FCSTD DOCUMENT  (FreeCAD 0.21R33694 (Git))
Label: merged-carcasa-final
License: Creative Commons Attribution-NonCommercial-ShareAlike 4.0
LicenseURL: https://creativecommons.org/licenses/by-nc-sa/4.0/
objects: TechDraw::DrawViewDimension×81, Part::Box×29, Part::Fuse×24, Part::Cut×21, TechDraw::DrawViewPart×20, Part::Feature×15, TechDraw::DrawViewBalloon×12, Part::Mirroring×11, Part::Chamfer×9, Part::Cylinder×6, Part::Fillet×5, TechDraw::DrawSVGTemplate×5, TechDraw::DrawPage×5, App::DocumentObjectGroup×5, Sketcher::SketchObject×4, Part::Extrusion×4, Part::Compound×3, TechDraw::DrawViewAnnotation×3, Part::MultiFuse×2, Part::FeaturePython×2, +5 more types
note: 228 computed .brp shape members not serialized (recipe doc carries the construction recipe); baked Part::Feature solids carry a one-line shape summary decoded from their .brp

FEATURE [Sketcher::SketchObject] Sketch  label="case-taladros"
  FullyConstrained = true
  MapMode = 5
  Support = -> [XY_Plane]
  sketch-geometry (4):
    g0: LineSegment StartX=-50 StartY=85 StartZ=0 EndX=50 EndY=85 EndZ=0
    g1: LineSegment StartX=50 StartY=85 StartZ=0 EndX=50 EndY=-85 EndZ=0
    g2: LineSegment StartX=50 StartY=-85 StartZ=0 EndX=-50 EndY=-85 EndZ=0
    g3: LineSegment StartX=-50 StartY=-85 StartZ=0 EndX=-50 EndY=85 EndZ=0
  constraints (10):
    c: Coincident(g0,g1)
    c: Coincident(g1,g2)
    c: Coincident(g2,g3)
    c: Coincident(g3,g0)
    c: Horizontal(g2)
    c: Vertical(g1)
    c: Symmetric(g0,g0,g-2)
    c: Symmetric(g2,g0,g-1)
    c: DistanceY(g3,g3) = 170
    c: DistanceX(g0,g0) = 100
FEATURE [Part::Box] Box001  label="vaciado"
  AttacherType = Attacher::AttachEngine3D
  Height = 42
  Length = 94
  Placement = pos=(-47,-76,3) rot=(0,0,1;0rad)
  Width = 152
FEATURE [Sketcher::SketchObject] Sketch008  label="tapa-taladros"
  FullyConstrained = true
  MapMode = 5
  sketch-geometry (4):
    g0: LineSegment StartX=-49 StartY=84 StartZ=0 EndX=49 EndY=84 EndZ=0
    g1: LineSegment StartX=49 StartY=84 StartZ=0 EndX=49 EndY=-84 EndZ=0
    g2: LineSegment StartX=49 StartY=-84 StartZ=0 EndX=-49 EndY=-84 EndZ=0
    g3: LineSegment StartX=-49 StartY=-84 StartZ=0 EndX=-49 EndY=84 EndZ=0
  constraints (10):
    c: Coincident(g0,g1)
    c: Coincident(g1,g2)
    c: Coincident(g2,g3)
    c: Coincident(g3,g0)
    c: Horizontal(g2)
    c: Vertical(g1)
    c: Symmetric(g0,g0,g-2)
    c: Symmetric(g2,g0,g-1)
    c: DistanceY(g3,g3) = 168
    c: DistanceX(g0,g0) = 98
FEATURE [Part::Box] Box010  label="restriccion-lipo"
  AttacherType = Attacher::AttachEngine3D
  Height = 38
  Length = 5
  Placement = pos=(17,-75,5) rot=(0,0,1;0rad)
  Width = 73
FEATURE [Part::Box] Box011  label="restriccion-lipo001"
  AttacherType = Attacher::AttachEngine3D
  Height = 18
  Length = 7
  Placement = pos=(16,-60,14) rot=(0,0,1;0rad)
  Width = 43
FEATURE [Part::Cut] Cut028
  Base = -> Box010
  Refine = true
  Tool = -> Box011
FEATURE [Part::Chamfer] Chamfer002
  Base = -> Cut028
  Edges = 2 edges r=3: [Edge2,Edge4]
FEATURE [Part::Chamfer] Chamfer003
  Base = -> Chamfer002
  Edges = 4 edges r=2: [Edge5,Edge6,Edge7,Edge8]
FEATURE [Part::Box] Box012  label="Cube004"
  AttacherType = Attacher::AttachEngine3D
  Height = 5
  Length = 20
  Placement = pos=(20,-4,16) rot=(0,0,1;0rad)
  Width = 2
FEATURE [Part::Fuse] Fusion001032  label="rejillas-lipo"
  Base = -> Chamfer003
  Placement = pos=(7,2,-2) rot=(0,0,1;0rad)
  Refine = true
  Tool = -> Box012
FEATURE [Part::Box] Box015  label="Cubo002"
  AttacherType = Attacher::AttachEngine3D
  Height = 4
  Length = 50
  Placement = pos=(-25,22,-7.5) rot=(0,0,1;0rad)
  Width = 30
FEATURE [Part::Box] Box016  label="cubo-corte"
  AttacherType = Attacher::AttachEngine3D
  Height = 20
  Length = 56
  Placement = pos=(-145,75,-20) rot=(0,0,1;0rad)
  Width = 16
FEATURE [Part::Cylinder] Cylinder007  label="Cilindro-movil"
  Angle = 360
  AttacherType = Attacher::AttachEngine3D
  FirstAngle = 0
  Height = 170
  Placement = pos=(-200,92,-6) rot=(0,1,0;1.5708rad)
  Radius = 3.5
  SecondAngle = 0
FEATURE [Part::Feature] Fusion001034  label="Rosca macho012"
  Placement = pos=(-17,27,-10) rot=(0,0,1;0rad)
  shape: bbox 3.919 x 4.387 x 44 mm, 35 faces (baked)
FEATURE [Part::Feature] Fusion001035  label="Rosca macho013"
  Placement = pos=(17,27,-10) rot=(0,0,1;0rad)
  shape: bbox 3.919 x 4.387 x 44 mm, 35 faces (baked)
FEATURE [Part::MultiFuse] Fusion001036
  Refine = true
  Shapes = -> [Fusion001034,Fusion001035]
FEATURE [Part::Cut] Cut030  label="Soporte_eje001"
  Base = -> Box015
  Placement = pos=(-117,38,0) rot=(0,0,1;0rad)
  Refine = true
  Tool = -> Fusion001036
FEATURE [Part::Feature] Fusion001037  label="Rosca macho014"
  Placement = pos=(-170,93.75,-8.78) rot=(0.819304,0.219813,-0.52955;0.936369rad)
  shape: bbox 4.221 x 33 x 32.52 mm, 35 faces (baked)
FEATURE [Part::Feature] Fusion001038  label="Rosca macho015"
  Placement = pos=(-60,93.75,-8.78) rot=(0.819304,0.219813,-0.52955;0.936369rad)
  shape: bbox 4.221 x 33 x 32.52 mm, 35 faces (baked)
FEATURE [Part::Fuse] Fusion001033  label="roscas002"
  Base = -> Fusion001037
  Refine = true
  Tool = -> Fusion001038
FEATURE [Part::Fuse] Fusion001039  label="cilindro-movil001"
  Base = -> Cut030
  Refine = true
  Tool = -> Cylinder007
FEATURE [Sketcher::SketchObject] Sketch009
  FullyConstrained = false
  MapMode = 5
  Placement = pos=(0,0,0) rot=(0.57735,0.57735,0.57735;2.0944rad)
  Support = -> [YZ_Plane004]
  sketch-geometry (9):
    g0: ArcOfCircle CenterX=0 CenterY=0 CenterZ=0 NormalX=0 NormalY=0 NormalZ=1 AngleXU=0 Radius=5.5 StartAngle=6.08579 EndAngle=9.70025
    g1: Circle CenterX=0 CenterY=-1.19343 CenterZ=0 NormalX=0 NormalY=0 NormalZ=1 AngleXU=0 Radius=4
    g2: LineSegment StartX=-2.36 StartY=4.37566 StartZ=0 EndX=2.36 EndY=4.37566 EndZ=0
    g3: LineSegment StartX=2.36 StartY=4.37566 StartZ=0 EndX=2.36 EndY=3.44566 EndZ=0
    g4: LineSegment StartX=2.36 StartY=3.44566 StartZ=0 EndX=-2.36 EndY=3.44566 EndZ=0
    g5: LineSegment StartX=-2.36 StartY=3.44566 StartZ=0 EndX=-2.36 EndY=4.37566 EndZ=0
    g6: LineSegment StartX=-5.29263 StartY=-1.49602 StartZ=0 EndX=-5.29263 EndY=-8 EndZ=0
    g7: LineSegment StartX=-5.29263 StartY=-8 StartZ=0 EndX=5.39319 EndY=-8 EndZ=0
    g8: LineSegment StartX=5.39319 StartY=-8 StartZ=0 EndX=5.39319 EndY=-1.07864 EndZ=0
  constraints (21):
    c: Coincident(g0,g-1)
    c: Coincident(g2,g3)
    c: Coincident(g3,g4)
    c: Coincident(g4,g5)
    c: Coincident(g5,g2)
    c: Horizontal(g4)
    c: Vertical(g3)
    c: Vertical(g5)
    c: Symmetric(g2,g2,g-2)
    c: PointOnObject(g1,g-2)
    c: Radius(g0) = 5.5
    c: Radius(g1) = 4
    c: DistanceY(g5,g5) = 0.93
    c: DistanceX(g2,g2) = 4.72
    c: Coincident(g6,g7)
    c: Coincident(g7,g8)
    c: Horizontal(g7)
    c: Vertical(g6)
    c: Vertical(g8)
    c: Coincident(g0,g8)
    c: Coincident(g6,g0)
FEATURE [Part::Extrusion] Extrude003  label="cilindro-fijo001"
  Base = -> Sketch009
  Dir = (1,-1e-16,1e-16)
  DirMode = 2
  FaceMakerClass = Part::FaceMakerBullseye
  LengthFwd = 170
  LengthRev = 0
  Placement = pos=(-200,91,-5) rot=(1,0,0;1.02974rad)
  Solid = true
  Symmetric = false
FEATURE [Part::Cut] Cut029
  Base = -> Extrude003
  Refine = true
  Tool = -> Fusion001033
FEATURE [Part::Cut] Cut031  label="fijacion-brazo"
  Base = -> Cut029
  Refine = true
  Tool = -> Box016
FEATURE [Part::Compound] Compound  label="brazo-mejorados"
  Links = -> [Cut031,Fusion001039]
  Placement = pos=(136,115,-16.54) rot=(0.259987,0.259987,0.929954;1.64236rad)
FEATURE [Part::Mirroring] Part__Mirroring014  label="brazo-mejorados (Mirror #13)"
  Base = (0,0,0)
  Normal = (1,0,0)
  Source = -> Compound
FEATURE [Part::Extrusion] Extrude  label="carcasa-extruida"
  Base = -> Sketch
  Dir = (0,0,1)
  DirMode = 2
  FaceMakerClass = Part::FaceMakerBullseye
  LengthFwd = 45
  LengthRev = 0
  Solid = true
  Symmetric = false
FEATURE [Part::Box] Box019  label="vaciado001"
  AttacherType = Attacher::AttachEngine3D
  Height = 42
  Length = 74
  Placement = pos=(-37,-82,3) rot=(0,0,1;0rad)
  Width = 164
FEATURE [Part::Cut] Cut
  Base = -> Extrude
  Refine = true
  Tool = -> Box001
FEATURE [Part::Cut] Cut034
  Base = -> Cut
  Refine = true
  Tool = -> Box019
FEATURE [Part::Chamfer] Chamfer
  Base = -> Cut034
  Edges = 4 edges r=1: [Edge4,Edge7,Edge10,Edge12]
FEATURE [Part::Chamfer] Chamfer005
  Base = -> Chamfer
  Edges = 12 edges r=1: [Edge20,Edge21,Edge22,Edge23,Edge24,Edge25,Edge26,Edge27,Edge28,Edge29,Edge30,Edge31]
FEATURE [Part::Fillet] Fillet  label="carcasa-chaflanada"
  Base = -> Chamfer005
  Edges = 4 edges r=2: [Edge75,Edge77,Edge79,Edge80]
FEATURE [Part::Fuse] Fusion001040  label="brazos-v2"
  Base = -> Compound
  Placement = pos=(0,0,-1) rot=(0,0,1;0rad)
  Refine = true
  Tool = -> Part__Mirroring014
FEATURE [Part::Extrusion] Extrude004
  Base = -> Sketch008
  Dir = (0,0,1)
  DirMode = 2
  FaceMakerClass = Part::FaceMakerBullseye
  LengthFwd = 25
  LengthRev = 0
  Placement = pos=(0,0,45) rot=(0,0,1;0rad)
  Solid = true
  Symmetric = false
FEATURE [Part::Chamfer] Chamfer006  label="tapa"
  Base = -> Extrude004
  Edges = 4 edges r=2: [Edge4,Edge7,Edge10,Edge12]
FEATURE [Part::Box] Box  label="Cube"
  AttacherType = Attacher::AttachEngine3D
  Height = 5
  Length = 10
  Width = 20
FEATURE [Part::Box] Box020  label="Cube001"
  AttacherType = Attacher::AttachEngine3D
  Height = 50
  Length = 5
  Placement = pos=(-5,0,0) rot=(0,0,1;0rad)
  Width = 20
FEATURE [Part::Box] Box002  label="Cube002"
  AttacherType = Attacher::AttachEngine3D
  Height = 50
  Length = 5
  Placement = pos=(-5,0,0) rot=(0,0,1;0rad)
  Width = 20
FEATURE [Part::Box] Box003  label="Cube003"
  AttacherType = Attacher::AttachEngine3D
  Height = 20
  Length = 10
  Placement = pos=(0,5,5) rot=(0,0,1;0rad)
  Width = 10
FEATURE [Part::Cylinder] Cylinder
  Angle = 360
  AttacherType = Attacher::AttachEngine3D
  FirstAngle = 0
  Height = 6
  Placement = pos=(5,10,0) rot=(0,0,1;0rad)
  Radius = 0.5
  SecondAngle = 0
FEATURE [Part::Fuse] Fusion001047
  Base = -> Box
  Refine = true
  Tool = -> Box020
FEATURE [Part::Fillet] Fillet001
  Base = -> Fusion001047
  Edges = 1 edges r=9.99: [Edge5]
FEATURE [Part::Cut] Cut035
  Base = -> Fillet001
  Refine = true
  Tool = -> Box002
FEATURE [Part::Cut] Cut001
  Base = -> Cut035
  Refine = true
  Tool = -> Box003
FEATURE [Part::Cut] Cut002  label="acople"
  Base = -> Cut001
  Refine = true
  Tool = -> Cylinder
FEATURE [Part::Feature] Fusion001001  label="Rosca macho002"
  Placement = pos=(5,10,-9) rot=(0,0,1;0rad)
  shape: bbox 3.919 x 4.387 x 44 mm, 35 faces (baked)
FEATURE [Part::Cut] Cut003  label="acople-roscado"
  Base = -> Cut002
  Placement = pos=(50,-85,5) rot=(0,0,1;0rad)
  Refine = true
  Tool = -> Fusion001001
FEATURE [Part::Mirroring] Part__Mirroring021  label="acople-roscado (Mirror #7)"
  Base = (0,0,0)
  Normal = (1,0,0)
  Source = -> Cut003
FEATURE [Part::Fuse] Fusion001048
  Base = -> Cut003
  Refine = true
  Tool = -> Part__Mirroring021
FEATURE [Part::Mirroring] Part__Mirroring022  label="Fusion001048 (Mirror #8)"
  Base = (0,0,0)
  Normal = (0,1,0)
  Source = -> Fusion001048
FEATURE [Part::Fuse] Fusion001049  label="acoples-flotador"
  Base = -> Fusion001048
  Refine = true
  Tool = -> Part__Mirroring022
FEATURE [Part::Feature] Compound002  label="simple-rosca"
  Placement = pos=(43,-80,30) rot=(0,0,1;0rad)
  shape: bbox 3.919 x 4.387 x 44 mm, 65 faces (baked)
FEATURE [Part::Mirroring] Part__Mirroring023  label="simple-rosca (Mirror #7)"
  Base = (0,0,0)
  Normal = (1,0,0)
  Source = -> Compound002
FEATURE [Part::Fuse] Fusion001050
  Base = -> Compound002
  Refine = true
  Tool = -> Part__Mirroring023
FEATURE [Part::Mirroring] Part__Mirroring024  label="roscas-4"
  Base = (0,0,0)
  Normal = (0,1,0)
  Source = -> Fusion001050
FEATURE [Part::Fuse] Fusion001051  label="roscas-carcasa"
  Base = -> Fusion001050
  Refine = true
  Tool = -> Part__Mirroring024
FEATURE [Part::Feature] Compound003  label="simple-rosca001"
  Placement = pos=(43,-80,30) rot=(0,0,1;0rad)
  shape: bbox 3.919 x 4.387 x 44 mm, 65 faces (baked)
FEATURE [Part::Mirroring] Part__Mirroring025  label="simple-rosca (Mirror #7)001"
  Base = (0,0,0)
  Normal = (1,0,0)
  Source = -> Compound003
FEATURE [Part::Fuse] Fusion001052
  Base = -> Compound003
  Refine = true
  Tool = -> Part__Mirroring025
FEATURE [Part::Mirroring] Part__Mirroring026  label="roscas-005"
  Base = (0,0,0)
  Normal = (0,1,0)
  Source = -> Fusion001052
FEATURE [Part::Fuse] Fusion001053  label="roscas-tapa"
  Base = -> Fusion001052
  Placement = pos=(0,0,14) rot=(0,0,1;0rad)
  Refine = true
  Tool = -> Part__Mirroring026
FEATURE [Part::Cut] Cut036  label="carcasa-roscada-15mm"
  Base = -> Fillet
  Refine = true
  Tool = -> Fusion001051
FEATURE [Part::Cut] Cut037  label="tapa-roscada-5mm"
  Base = -> Chamfer006
  Placement = pos=(0,0,25) rot=(0,0,1;0rad)
  Refine = true
  Tool = -> Fusion001053
FEATURE [Part::Box] Box021  label="agujeros-new"
  AttacherType = Attacher::AttachEngine3D
  Height = 10
  Length = 10
  Placement = pos=(43,0,33) rot=(0,0,1;0rad)
  Width = 25
FEATURE [Part::Mirroring] Part__Mirroring027  label="agujeros-new (Mirror #11)"
  Base = (0,0,0)
  Normal = (1,0,0)
  Source = -> Box021
FEATURE [Part::Fuse] Fusion001054  label="agujeros-rectangulares"
  Base = -> Box021
  Refine = true
  Tool = -> Part__Mirroring027
FEATURE [Part::Box] Box024  label="receptor-space"
  AttacherType = Attacher::AttachEngine3D
  Height = 42
  Length = 25
  Placement = pos=(-47,68,3) rot=(0,0,-1;1.5708rad)
  Width = 2
FEATURE [PartDesign::FeatureBase] BaseFeature
  BaseFeature = -> Box024
FEATURE [PartDesign::Body] Body  label="carcasa-boceto"
  BaseFeature = -> Box024
  Group = -> [BaseFeature,Sketch]
  Origin = -> Origin
  Tip = -> BaseFeature
FEATURE [Part::Box] Box025  label="vaciado002"
  AttacherType = Attacher::AttachEngine3D
  Height = 3
  Length = 94
  Placement = pos=(-47,-76,70) rot=(0,0,1;0rad)
  Width = 152
FEATURE [Part::Cut] Cut038  label="tapa-roscada-5mm001"
  Base = -> Cut037
  Placement = pos=(0,0,-25) rot=(0,0,1;0rad)
  Refine = true
  Tool = -> Box025
FEATURE [Part::Fuse] Fusion
  Base = -> Fusion001049
  Refine = true
  Tool = -> Cut036
FEATURE [Part::Fuse] Fusion001055
  Base = -> Fusion001040
  Refine = true
  Tool = -> Fusion
FEATURE [Part::Cut] Cut039  label="carcasa-fusionada"
  Base = -> Fusion001055
  Refine = true
  Tool = -> Fusion001054
FEATURE [Part::Chamfer] Chamfer007
  Base = -> Cut039
  Edges = 3 edges r=1: [Edge393,Edge397,Edge398]
FEATURE [Part::Chamfer] Chamfer008
  Base = -> Chamfer007
  Edges = 3 edges r=1: [Edge341,Edge342,Edge344]
FEATURE [Part::Fuse] Fusion001056  label="carcasa-merged"
  Base = -> Fusion001032
  Refine = true
  Tool = -> Chamfer008
FEATURE [Part::Compound] Compound004  label="carcasa-compound"
  Links = -> [Fusion001056]
FEATURE [TechDraw::DrawSVGTemplate] Template002
  Height = 297
  Orientation = 1
  Template = <path>
  Width = 420
FEATURE [TechDraw::DrawViewAnnotation] Annotation  label="índice"
  Font = osifont
  LineSpace = 100
  LockPosition = false
  MaxWidth = -1
  Rotation = 0
  ScaleType = 0
  Text = 1: Varilla móvil | 2: Acoples flotador | 3: Unión brazo | 4: Agujero cableado
  TextSize = 5
  TextStyle = 0
  X = 258.993
  Y = 115.362
FEATURE [Part::Box] Box026  label="Cubo003"
  AttacherType = Attacher::AttachEngine3D
  Height = 4
  Length = 50
  Placement = pos=(-25,22,-7.5) rot=(0,0,1;0rad)
  Width = 30
FEATURE [Part::Box] Box027  label="cubo-corte001"
  AttacherType = Attacher::AttachEngine3D
  Height = 20
  Length = 56
  Placement = pos=(-145,75,-20) rot=(0,0,1;0rad)
  Width = 16
FEATURE [Part::Cylinder] Cylinder008  label="Cilindro-movil001"
  Angle = 360
  AttacherType = Attacher::AttachEngine3D
  FirstAngle = 0
  Height = 170
  Placement = pos=(-200,92,-6) rot=(0,1,0;1.5708rad)
  Radius = 3.5
  SecondAngle = 0
FEATURE [Part::Feature] Fusion001058  label="Rosca macho016"
  Placement = pos=(-17,27,-10) rot=(0,0,1;0rad)
  shape: bbox 3.919 x 4.387 x 44 mm, 35 faces (baked)
FEATURE [Part::Feature] Fusion001059  label="Rosca macho017"
  Placement = pos=(17,27,-10) rot=(0,0,1;0rad)
  shape: bbox 3.919 x 4.387 x 44 mm, 35 faces (baked)
FEATURE [Part::MultiFuse] Fusion001060
  Refine = true
  Shapes = -> [Fusion001058,Fusion001059]
FEATURE [Part::Cut] Cut041  label="Soporte_eje002"
  Base = -> Box026
  Placement = pos=(-117,38,0) rot=(0,0,1;0rad)
  Refine = true
  Tool = -> Fusion001060
FEATURE [Part::Feature] Fusion001061  label="Rosca macho018"
  Placement = pos=(-170,93.75,-8.78) rot=(0.819304,0.219813,-0.52955;0.936369rad)
  shape: bbox 4.221 x 33 x 32.52 mm, 35 faces (baked)
FEATURE [Part::Feature] Fusion001062  label="Rosca macho019"
  Placement = pos=(-60,93.75,-8.78) rot=(0.819304,0.219813,-0.52955;0.936369rad)
  shape: bbox 4.221 x 33 x 32.52 mm, 35 faces (baked)
FEATURE [Part::Fuse] Fusion001057  label="roscas003"
  Base = -> Fusion001061
  Refine = true
  Tool = -> Fusion001062
FEATURE [Part::Fuse] Fusion001063  label="cilindro-movil002"
  Base = -> Cut041
  Refine = true
  Tool = -> Cylinder008
FEATURE [Sketcher::SketchObject] Sketch010
  FullyConstrained = false
  MapMode = 5
  Placement = pos=(0,0,0) rot=(0.57735,0.57735,0.57735;2.0944rad)
  Support = -> [YZ_Plane005]
  sketch-geometry (9):
    g0: ArcOfCircle CenterX=0 CenterY=0 CenterZ=0 NormalX=0 NormalY=0 NormalZ=1 AngleXU=0 Radius=5.5 StartAngle=6.08579 EndAngle=9.70025
    g1: Circle CenterX=0 CenterY=-1.19343 CenterZ=0 NormalX=0 NormalY=0 NormalZ=1 AngleXU=0 Radius=4
    g2: LineSegment StartX=-2.36 StartY=4.37566 StartZ=0 EndX=2.36 EndY=4.37566 EndZ=0
    g3: LineSegment StartX=2.36 StartY=4.37566 StartZ=0 EndX=2.36 EndY=3.44566 EndZ=0
    g4: LineSegment StartX=2.36 StartY=3.44566 StartZ=0 EndX=-2.36 EndY=3.44566 EndZ=0
    g5: LineSegment StartX=-2.36 StartY=3.44566 StartZ=0 EndX=-2.36 EndY=4.37566 EndZ=0
    g6: LineSegment StartX=-5.29263 StartY=-1.49602 StartZ=0 EndX=-5.29263 EndY=-8 EndZ=0
    g7: LineSegment StartX=-5.29263 StartY=-8 StartZ=0 EndX=5.39319 EndY=-8 EndZ=0
    g8: LineSegment StartX=5.39319 StartY=-8 StartZ=0 EndX=5.39319 EndY=-1.07864 EndZ=0
  constraints (21):
    c: Coincident(g0,g-1)
    c: Coincident(g2,g3)
    c: Coincident(g3,g4)
    c: Coincident(g4,g5)
    c: Coincident(g5,g2)
    c: Horizontal(g4)
    c: Vertical(g3)
    c: Vertical(g5)
    c: Symmetric(g2,g2,g-2)
    c: PointOnObject(g1,g-2)
    c: Radius(g0) = 5.5
    c: Radius(g1) = 4
    c: DistanceY(g5,g5) = 0.93
    c: DistanceX(g2,g2) = 4.72
    c: Coincident(g6,g7)
    c: Coincident(g7,g8)
    c: Horizontal(g7)
    c: Vertical(g6)
    c: Vertical(g8)
    c: Coincident(g0,g8)
    c: Coincident(g6,g0)
FEATURE [Part::Extrusion] Extrude005  label="cilindro-fijo002"
  Base = -> Sketch010
  Dir = (1,-1e-16,1e-16)
  DirMode = 2
  FaceMakerClass = Part::FaceMakerBullseye
  LengthFwd = 170
  LengthRev = 0
  Placement = pos=(-200,91,-5) rot=(1,0,0;1.02974rad)
  Solid = true
  Symmetric = false
FEATURE [Part::Cut] Cut040
  Base = -> Extrude005
  Refine = true
  Tool = -> Fusion001057
FEATURE [Part::Cut] Cut042  label="fijacion-brazo001"
  Base = -> Cut040
  Refine = true
  Tool = -> Box027
FEATURE [Part::Compound] Compound006  label="brazo-mejorados001"
  Links = -> [Cut042,Fusion001063]
  Placement = pos=(136,115,-16.54) rot=(0.259987,0.259987,0.929954;1.64236rad)
FEATURE [TechDraw::DrawViewPart] View003  label="brazo-aumentado"
  CoarseView = true
  Direction = (0,-1,0)
  Focus = 100
  HardHidden = false
  IsoCount = 0
  IsoHidden = false
  IsoVisible = false
  LockPosition = false
  Perspective = false
  Rotation = 0
  Scale = 3
  ScaleType = 2
  ScrubCount = 0
  SeamHidden = false
  SeamVisible = false
  SmoothHidden = true
  SmoothVisible = true
  Source = -> [Compound006]
  X = 350
  XDirection = (1,0,0)
  Y = 120
FEATURE [TechDraw::DrawViewDimension] Dimension030
  AngleOverride = false
  Arbitrary = false
  ArbitraryTolerances = false
  EqualTolerance = true
  ExtensionAngle = 0
  FormatSpec = %.2w
  FormatSpecOverTolerance = %+.2w
  FormatSpecUnderTolerance = %+.2w
  Inverted = false
  LineAngle = 0
  LockPosition = false
  MeasureType = 1
  OverTolerance = 0
  References2D = -> [View003]
  Rotation = 0
  ScaleType = 0
  TheoreticalExact = false
  Type = 2
  UnderTolerance = 0
  X = 0.954765
  Y = 21.9542
FEATURE [TechDraw::DrawViewDimension] Dimension031
  AngleOverride = false
  Arbitrary = false
  ArbitraryTolerances = false
  EqualTolerance = true
  ExtensionAngle = 0
  FormatSpec = %.2w
  FormatSpecOverTolerance = %+.2w
  FormatSpecUnderTolerance = %+.2w
  Inverted = false
  LineAngle = 0
  LockPosition = false
  MeasureType = 1
  OverTolerance = 0
  References2D = -> [View003]
  Rotation = 0
  ScaleType = 0
  TheoreticalExact = false
  Type = 1
  UnderTolerance = 0
  X = -18.1497
  Y = -5.21324
FEATURE [TechDraw::DrawViewDimension] Dimension032
  AngleOverride = false
  Arbitrary = false
  ArbitraryTolerances = false
  EqualTolerance = true
  ExtensionAngle = 0
  FormatSpec = %.2w
  FormatSpecOverTolerance = %+.2w
  FormatSpecUnderTolerance = %+.2w
  Inverted = false
  LineAngle = 0
  LockPosition = false
  MeasureType = 1
  OverTolerance = 0
  References2D = -> [View003]
  Rotation = 0
  ScaleType = 0
  TheoreticalExact = false
  Type = 2
  UnderTolerance = 0
  X = -65.909
  Y = 19.0353
FEATURE [TechDraw::DrawViewDimension] Dimension033
  AngleOverride = false
  Arbitrary = false
  ArbitraryTolerances = false
  EqualTolerance = true
  ExtensionAngle = 0
  FormatSpec = %.2w
  FormatSpecOverTolerance = %+.2w
  FormatSpecUnderTolerance = %+.2w
  Inverted = false
  LineAngle = 0
  LockPosition = false
  MeasureType = 1
  OverTolerance = 0
  References2D = -> [View003]
  Rotation = 0
  ScaleType = 0
  TheoreticalExact = false
  Type = 1
  UnderTolerance = 0
  X = -43.6049
  Y = -1.6808
FEATURE [TechDraw::DrawViewDimension] Dimension034
  AngleOverride = true
  Arbitrary = false
  ArbitraryTolerances = false
  EqualTolerance = true
  ExtensionAngle = 176.049
  FormatSpec = %.2w
  FormatSpecOverTolerance = %+.2w
  FormatSpecUnderTolerance = %+.2w
  Inverted = false
  LineAngle = 1.50337
  LockPosition = false
  MeasureType = 1
  OverTolerance = 0
  References2D = -> [View003]
  Rotation = 0
  ScaleType = 0
  TheoreticalExact = false
  Type = 0
  UnderTolerance = 0
  X = -11.1483
  Y = 9.51408
FEATURE [TechDraw::DrawViewBalloon] Balloon
  BubbleShape = 0
  EndType = 0
  EndTypeScale = 1
  KinkLength = 5
  LockPosition = false
  OriginX = -11.1483
  OriginY = 9.51408
  Rotation = 0
  ScaleType = 0
  ShapeScale = 1
  SourceView = -> View003
  Text = 3,5⌀
  TextWrapLen = -1
  X = -3.16715
  Y = 14.8662
FEATURE [TechDraw::DrawViewBalloon] Balloon001
  BubbleShape = 0
  EndType = 0
  EndTypeScale = 1
  KinkLength = 5
  LockPosition = false
  OriginX = -13.1465
  OriginY = 9.63488
  Rotation = 0
  ScaleType = 0
  ShapeScale = 1
  SourceView = -> View003
  Text = 4⌀
  TextWrapLen = -1
  X = -24.7117
  Y = 13.9011
FEATURE [TechDraw::DrawViewBalloon] Balloon004
  BubbleShape = 0
  EndType = 0
  EndTypeScale = 1
  KinkLength = 5
  LockPosition = false
  OriginX = 71.3845
  OriginY = -122.514
  Rotation = 0
  ScaleType = 0
  ShapeScale = 1
  Text = 3
  TextWrapLen = -1
  X = 113.884
  Y = -76.3509
FEATURE [TechDraw::DrawSVGTemplate] Template
  Height = 297
  Orientation = 1
  Template = <path>
  Width = 420
FEATURE [Mesh::Feature] Arduino_Bumper_0005  label="Arduino-uno-case"
  Placement = pos=(-19,-40,5) rot=(0,0,1;-1.5708rad)
FEATURE [Part::Box] Box028  label="restriccion-lipo002"
  AttacherType = Attacher::AttachEngine3D
  Height = 38
  Length = 5
  Placement = pos=(17,-75,5) rot=(0,0,1;0rad)
  Width = 73
FEATURE [Part::Box] Box029  label="restriccion-lipo003"
  AttacherType = Attacher::AttachEngine3D
  Height = 18
  Length = 7
  Placement = pos=(16,-60,14) rot=(0,0,1;0rad)
  Width = 43
FEATURE [Part::Box] Box030  label="Cube005"
  AttacherType = Attacher::AttachEngine3D
  Height = 5
  Length = 20
  Placement = pos=(20,-4,16) rot=(0,0,1;0rad)
  Width = 2
FEATURE [Part::Box] Box013  label="PDB-space"
  AttacherType = Attacher::AttachEngine3D
  Height = 3
  Length = 36
  Placement = pos=(25,54,3) rot=(0,0,1;3.14159rad)
  Width = 56
FEATURE [Part::Box] Box014  label="free-space"
  AttacherType = Attacher::AttachEngine3D
  Height = 42
  Length = 46.3
  Placement = pos=(-48,77,3) rot=(0,0,-1;1.5708rad)
  Width = 53
FEATURE [Part::Box] Box022  label="lipo-space"
  AttacherType = Attacher::AttachEngine3D
  Height = 36
  Length = 73
  Placement = pos=(30,-3,3) rot=(0,0,-1;1.5708rad)
  Width = 17
FEATURE [Part::Box] Box023  label="arduino-mega-space"
  AttacherType = Attacher::AttachEngine3D
  Height = 3
  Length = 53.3
  Placement = pos=(-45.15,-73.26,8) rot=(0,0,1;0rad)
  Width = 101.52
FEATURE [Part::Box] Box031  label="receptor-space001"
  AttacherType = Attacher::AttachEngine3D
  Height = 42
  Length = 25
  Placement = pos=(-47,68,3) rot=(0,0,-1;1.5708rad)
  Width = 2
FEATURE [Part::Feature] Compound001  label="pcb-support"
  Placement = pos=(25,54,3) rot=(0,0,1;3.14159rad)
  shape: bbox 40 x 56.1 x 12 mm, 27565 faces, 3 solids (baked)
FEATURE [Part::Feature] Compound007  label="arduino-mega-case-solid"
  Placement = pos=(-62,80,3) rot=(0,0,-1;1.5708rad)
  shape: bbox 57.6 x 106.6 x 5.8 mm, 182 faces (baked)
FEATURE [Part::Cut] Cut043
  Base = -> Box028
  Refine = true
  Tool = -> Box029
FEATURE [Part::Chamfer] Chamfer009
  Base = -> Cut043
  Edges = 2 edges r=3: [Edge2,Edge4]
FEATURE [Part::Chamfer] Chamfer010
  Base = -> Chamfer009
  Edges = 4 edges r=2: [Edge5,Edge6,Edge7,Edge8]
FEATURE [Part::Fuse] Fusion001064  label="rejillas-lipo001"
  Base = -> Chamfer010
  Placement = pos=(7,2,-2) rot=(0,0,1;0rad)
  Refine = true
  Tool = -> Box030
FEATURE [App::LinkGroup] LinkGroup  label="componentes-shell"
  ElementList = -> [Compound001,Box013,Box014,Fusion001064,Arduino_Bumper_0005,Compound007,Box022,Box023,Box031]
  LinkMode = 0
FEATURE [TechDraw::DrawViewPart] View004  label="Alzado001"
  CoarseView = true
  Direction = (0,-1,0)
  Focus = 100
  HardHidden = false
  IsoCount = 0
  IsoHidden = false
  IsoVisible = false
  LockPosition = false
  Perspective = false
  Rotation = 0
  Scale = 2
  ScaleType = 2
  ScrubCount = 0
  SeamHidden = false
  SeamVisible = false
  SmoothHidden = false
  SmoothVisible = true
  Source = -> [Compound007]
  X = 85
  XDirection = (1,0,0)
  Y = 260
FEATURE [TechDraw::DrawViewPart] View005  label="Planta001"
  CoarseView = true
  Direction = (0,0,1)
  Focus = 100
  HardHidden = false
  IsoCount = 0
  IsoHidden = false
  IsoVisible = false
  LockPosition = false
  Perspective = false
  Rotation = 0
  Scale = 2
  ScaleType = 2
  ScrubCount = 0
  SeamHidden = false
  SeamVisible = false
  SmoothHidden = false
  SmoothVisible = true
  Source = -> [Compound007]
  X = 85
  XDirection = (1,0,0)
  Y = 120
FEATURE [TechDraw::DrawViewPart] View006  label="Perfil001"
  CoarseView = true
  Direction = (1,0,0)
  Focus = 100
  HardHidden = false
  IsoCount = 0
  IsoHidden = false
  IsoVisible = false
  LockPosition = false
  Perspective = false
  Rotation = 0
  Scale = 2
  ScaleType = 2
  ScrubCount = 0
  SeamHidden = false
  SeamVisible = false
  SmoothHidden = false
  SmoothVisible = true
  Source = -> [Compound007]
  X = 270
  XDirection = (0,1,0)
  Y = 260
FEATURE [TechDraw::DrawViewPart] View007  label="Vista3D"
  CoarseView = true
  Direction = (0.57735,-0.57735,0.57735)
  Focus = 100
  HardHidden = false
  IsoCount = 0
  IsoHidden = false
  IsoVisible = false
  LockPosition = false
  Perspective = false
  Rotation = 0
  Scale = 2
  ScaleType = 2
  ScrubCount = 0
  SeamHidden = false
  SeamVisible = false
  SmoothHidden = false
  SmoothVisible = true
  Source = -> [Compound007]
  X = 270
  XDirection = (0.707107,0.707107,0)
  Y = 145
FEATURE [TechDraw::DrawViewDimension] Dimension035
  AngleOverride = false
  Arbitrary = false
  ArbitraryTolerances = false
  EqualTolerance = true
  ExtensionAngle = 0
  FormatSpec = %.2w
  FormatSpecOverTolerance = %+.2w
  FormatSpecUnderTolerance = %+.2w
  Inverted = false
  LineAngle = 0
  LockPosition = false
  MeasureType = 1
  OverTolerance = 0
  References2D = -> [View004]
  Rotation = 0
  ScaleType = 0
  TheoreticalExact = false
  Type = 1
  UnderTolerance = 0
  X = -56.5955
  Y = -11.5035
FEATURE [TechDraw::DrawViewDimension] Dimension036
  AngleOverride = false
  Arbitrary = false
  ArbitraryTolerances = false
  EqualTolerance = true
  ExtensionAngle = 0
  FormatSpec = %.2w
  FormatSpecOverTolerance = %+.2w
  FormatSpecUnderTolerance = %+.2w
  Inverted = false
  LineAngle = 0
  LockPosition = false
  MeasureType = 1
  OverTolerance = 0
  References2D = -> [View004]
  Rotation = 0
  ScaleType = 0
  TheoreticalExact = false
  Type = 1
  UnderTolerance = 0
  X = -15.6231
  Y = 18.1442
FEATURE [TechDraw::DrawViewDimension] Dimension037
  AngleOverride = false
  Arbitrary = false
  ArbitraryTolerances = false
  EqualTolerance = true
  ExtensionAngle = 0
  FormatSpec = %.2w
  FormatSpecOverTolerance = %+.2w
  FormatSpecUnderTolerance = %+.2w
  Inverted = false
  LineAngle = 0
  LockPosition = false
  MeasureType = 1
  OverTolerance = 0
  References2D = -> [View004]
  Rotation = 0
  ScaleType = 0
  TheoreticalExact = false
  Type = 1
  UnderTolerance = 0
  X = 39.8638
  Y = 18.4883
FEATURE [TechDraw::DrawViewDimension] Dimension038
  AngleOverride = false
  Arbitrary = false
  ArbitraryTolerances = false
  EqualTolerance = true
  ExtensionAngle = 0
  FormatSpec = %.2w
  FormatSpecOverTolerance = %+.2w
  FormatSpecUnderTolerance = %+.2w
  Inverted = false
  LineAngle = 0
  LockPosition = false
  MeasureType = 1
  OverTolerance = 0
  References2D = -> [View004]
  Rotation = 0
  ScaleType = 0
  TheoreticalExact = false
  Type = 1
  UnderTolerance = 0
  X = 27.5145
  Y = 26.668
FEATURE [TechDraw::DrawViewDimension] Dimension039
  AngleOverride = false
  Arbitrary = false
  ArbitraryTolerances = false
  EqualTolerance = true
  ExtensionAngle = 0
  FormatSpec = %.2w
  FormatSpecOverTolerance = %+.2w
  FormatSpecUnderTolerance = %+.2w
  Inverted = false
  LineAngle = 0
  LockPosition = false
  MeasureType = 1
  OverTolerance = 0
  References2D = -> [View004]
  Rotation = 0
  ScaleType = 0
  TheoreticalExact = false
  Type = 2
  UnderTolerance = 0
  X = -68.1854
  Y = 1.21884
FEATURE [TechDraw::DrawViewDimension] Dimension040
  AngleOverride = false
  Arbitrary = false
  ArbitraryTolerances = false
  EqualTolerance = true
  ExtensionAngle = 0
  FormatSpec = %.2w
  FormatSpecOverTolerance = %+.2w
  FormatSpecUnderTolerance = %+.2w
  Inverted = false
  LineAngle = 0
  LockPosition = false
  MeasureType = 1
  OverTolerance = 0
  References2D = -> [View004]
  Rotation = 0
  ScaleType = 0
  TheoreticalExact = false
  Type = 1
  UnderTolerance = 0
  X = 62.0579
  Y = 17.0449
FEATURE [TechDraw::DrawViewDimension] Dimension041
  AngleOverride = false
  Arbitrary = false
  ArbitraryTolerances = false
  EqualTolerance = true
  ExtensionAngle = 0
  FormatSpec = %.2w
  FormatSpecOverTolerance = %+.2w
  FormatSpecUnderTolerance = %+.2w
  Inverted = false
  LineAngle = 0
  LockPosition = false
  MeasureType = 1
  OverTolerance = 0
  References2D = -> [View005]
  Rotation = 0
  ScaleType = 0
  TheoreticalExact = false
  Type = 2
  UnderTolerance = 0
  X = 61.359
  Y = 7.1241
FEATURE [TechDraw::DrawViewDimension] Dimension042
  AngleOverride = false
  Arbitrary = false
  ArbitraryTolerances = false
  EqualTolerance = true
  ExtensionAngle = 0
  FormatSpec = %.2w
  FormatSpecOverTolerance = %+.2w
  FormatSpecUnderTolerance = %+.2w
  Inverted = false
  LineAngle = 0
  LockPosition = false
  MeasureType = 1
  OverTolerance = 0
  References2D = -> [View005]
  Rotation = 0
  ScaleType = 0
  TheoreticalExact = false
  Type = 2
  UnderTolerance = 0
  X = 58.8554
  Y = 114.866
FEATURE [TechDraw::DrawViewDimension] Dimension043
  AngleOverride = false
  Arbitrary = false
  ArbitraryTolerances = false
  EqualTolerance = true
  ExtensionAngle = 0
  FormatSpec = %.2w
  FormatSpecOverTolerance = %+.2w
  FormatSpecUnderTolerance = %+.2w
  Inverted = false
  LineAngle = 0
  LockPosition = false
  MeasureType = 1
  OverTolerance = 0
  References2D = -> [View005]
  Rotation = 0
  ScaleType = 0
  TheoreticalExact = false
  Type = 1
  UnderTolerance = 0
  X = -8.69266
  Y = 102.119
FEATURE [TechDraw::DrawViewDimension] Dimension044
  AngleOverride = false
  Arbitrary = false
  ArbitraryTolerances = false
  EqualTolerance = true
  ExtensionAngle = 0
  FormatSpec = %.2w
  FormatSpecOverTolerance = %+.2w
  FormatSpecUnderTolerance = %+.2w
  Inverted = false
  LineAngle = 0
  LockPosition = false
  MeasureType = 1
  OverTolerance = 0
  References2D = -> [View005]
  Rotation = 0
  ScaleType = 0
  TheoreticalExact = false
  Type = 1
  UnderTolerance = 0
  X = 45.2
  Y = 100.89
FEATURE [TechDraw::DrawViewDimension] Dimension045
  AngleOverride = false
  Arbitrary = false
  ArbitraryTolerances = false
  EqualTolerance = true
  ExtensionAngle = 0
  FormatSpec = %.2w
  FormatSpecOverTolerance = %+.2w
  FormatSpecUnderTolerance = %+.2w
  Inverted = false
  LineAngle = 0
  LockPosition = false
  MeasureType = 1
  OverTolerance = 0
  References2D = -> [View005]
  Rotation = 0
  ScaleType = 0
  TheoreticalExact = false
  Type = 1
  UnderTolerance = 0
  X = -50.8147
  Y = 98.7384
FEATURE [TechDraw::DrawViewDimension] Dimension046
  AngleOverride = false
  Arbitrary = false
  ArbitraryTolerances = false
  EqualTolerance = true
  ExtensionAngle = 0
  FormatSpec = %.2w
  FormatSpecOverTolerance = %+.2w
  FormatSpecUnderTolerance = %+.2w
  Inverted = false
  LineAngle = 0
  LockPosition = false
  MeasureType = 1
  OverTolerance = 0
  References2D = -> [View005]
  Rotation = 0
  ScaleType = 0
  TheoreticalExact = false
  Type = 2
  UnderTolerance = 0
  X = -43.6915
  Y = 114.752
FEATURE [TechDraw::DrawViewDimension] Dimension047
  AngleOverride = false
  Arbitrary = false
  ArbitraryTolerances = false
  EqualTolerance = true
  ExtensionAngle = 0
  FormatSpec = %.2w
  FormatSpecOverTolerance = %+.2w
  FormatSpecUnderTolerance = %+.2w
  Inverted = false
  LineAngle = 0
  LockPosition = false
  MeasureType = 1
  OverTolerance = 0
  References2D = -> [View005]
  Rotation = 0
  ScaleType = 0
  TheoreticalExact = false
  Type = 2
  UnderTolerance = 0
  X = -39.9933
  Y = 4.09981
FEATURE [TechDraw::DrawViewDimension] Dimension048
  AngleOverride = false
  Arbitrary = false
  ArbitraryTolerances = false
  EqualTolerance = true
  ExtensionAngle = 0
  FormatSpec = %.2w
  FormatSpecOverTolerance = %+.2w
  FormatSpecUnderTolerance = %+.2w
  Inverted = false
  LineAngle = 0
  LockPosition = false
  MeasureType = 1
  OverTolerance = 0
  References2D = -> [View005]
  Rotation = 0
  ScaleType = 0
  TheoreticalExact = false
  Type = 2
  UnderTolerance = 0
  X = -68.7669
  Y = 3.91103
FEATURE [TechDraw::DrawViewDimension] Dimension049
  AngleOverride = false
  Arbitrary = false
  ArbitraryTolerances = false
  EqualTolerance = true
  ExtensionAngle = 0
  FormatSpec = %.2w
  FormatSpecOverTolerance = %+.2w
  FormatSpecUnderTolerance = %+.2w
  Inverted = false
  LineAngle = 0
  LockPosition = false
  MeasureType = 1
  OverTolerance = 0
  References2D = -> [View005]
  Rotation = 0
  ScaleType = 0
  TheoreticalExact = false
  Type = 1
  UnderTolerance = 0
  X = -12.3165
  Y = -88.0736
FEATURE [TechDraw::DrawViewDimension] Dimension051
  AngleOverride = false
  Arbitrary = false
  ArbitraryTolerances = false
  EqualTolerance = true
  ExtensionAngle = 0
  FormatSpec = %.2w
  FormatSpecOverTolerance = %+.2w
  FormatSpecUnderTolerance = %+.2w
  Inverted = false
  LineAngle = 0
  LockPosition = false
  MeasureType = 1
  OverTolerance = 0
  References2D = -> [View005]
  Rotation = 0
  ScaleType = 0
  TheoreticalExact = false
  Type = 2
  UnderTolerance = 0
  X = -65.2512
  Y = -102.283
FEATURE [TechDraw::DrawViewDimension] Dimension052
  AngleOverride = false
  Arbitrary = false
  ArbitraryTolerances = false
  EqualTolerance = true
  ExtensionAngle = 0
  FormatSpec = %.2w
  FormatSpecOverTolerance = %+.2w
  FormatSpecUnderTolerance = %+.2w
  Inverted = false
  LineAngle = 0
  LockPosition = false
  MeasureType = 1
  OverTolerance = 0
  References2D = -> [View005]
  Rotation = 0
  ScaleType = 0
  TheoreticalExact = false
  Type = 2
  UnderTolerance = 0
  X = 79.1059
  Y = -100.212
FEATURE [TechDraw::DrawViewDimension] Dimension053
  AngleOverride = false
  Arbitrary = false
  ArbitraryTolerances = false
  EqualTolerance = true
  ExtensionAngle = 0
  FormatSpec = %.2w
  FormatSpecOverTolerance = %+.2w
  FormatSpecUnderTolerance = %+.2w
  Inverted = false
  LineAngle = 0
  LockPosition = false
  MeasureType = 1
  OverTolerance = 0
  References2D = -> [View005]
  Rotation = 0
  ScaleType = 0
  TheoreticalExact = false
  Type = 2
  UnderTolerance = 0
  X = 91.8793
  Y = -95.6917
FEATURE [TechDraw::DrawViewDimension] Dimension054
  AngleOverride = false
  Arbitrary = false
  ArbitraryTolerances = false
  EqualTolerance = true
  ExtensionAngle = 0
  FormatSpec = %.2w
  FormatSpecOverTolerance = %+.2w
  FormatSpecUnderTolerance = %+.2w
  Inverted = false
  LineAngle = 0
  LockPosition = false
  MeasureType = 1
  OverTolerance = 0
  References2D = -> [View005]
  Rotation = 0
  ScaleType = 0
  TheoreticalExact = false
  Type = 1
  UnderTolerance = 0
  X = 40
  Y = -85.0322
FEATURE [TechDraw::DrawViewDimension] Dimension055
  AngleOverride = false
  Arbitrary = false
  ArbitraryTolerances = false
  EqualTolerance = true
  ExtensionAngle = 0
  FormatSpec = %.2w
  FormatSpecOverTolerance = %+.2w
  FormatSpecUnderTolerance = %+.2w
  Inverted = false
  LineAngle = 0
  LockPosition = false
  MeasureType = 1
  OverTolerance = 0
  References2D = -> [View006]
  Rotation = 0
  ScaleType = 0
  TheoreticalExact = false
  Type = 1
  UnderTolerance = 0
  X = 1.14678
  Y = -19.3125
FEATURE [TechDraw::DrawViewDimension] Dimension056
  AngleOverride = false
  Arbitrary = false
  ArbitraryTolerances = false
  EqualTolerance = true
  ExtensionAngle = 0
  FormatSpec = %.2w
  FormatSpecOverTolerance = %+.2w
  FormatSpecUnderTolerance = %+.2w
  Inverted = false
  LineAngle = 0
  LockPosition = false
  MeasureType = 1
  OverTolerance = 0
  References2D = -> [View006]
  Rotation = 0
  ScaleType = 0
  TheoreticalExact = false
  Type = 1
  UnderTolerance = 0
  X = -103.6
  Y = 20.6339
FEATURE [TechDraw::DrawViewDimension] Dimension057
  AngleOverride = false
  Arbitrary = false
  ArbitraryTolerances = false
  EqualTolerance = true
  ExtensionAngle = 0
  FormatSpec = %.2w
  FormatSpecOverTolerance = %+.2w
  FormatSpecUnderTolerance = %+.2w
  Inverted = false
  LineAngle = 0
  LockPosition = false
  MeasureType = 1
  OverTolerance = 0
  References2D = -> [View006]
  Rotation = 0
  ScaleType = 0
  TheoreticalExact = false
  Type = 1
  UnderTolerance = 0
  X = -90.6331
  Y = 18.4567
FEATURE [TechDraw::DrawViewDimension] Dimension058
  AngleOverride = false
  Arbitrary = false
  ArbitraryTolerances = false
  EqualTolerance = true
  ExtensionAngle = 0
  FormatSpec = %.2w
  FormatSpecOverTolerance = %+.2w
  FormatSpecUnderTolerance = %+.2w
  Inverted = false
  LineAngle = 0
  LockPosition = false
  MeasureType = 1
  OverTolerance = 0
  References2D = -> [View006]
  Rotation = 0
  ScaleType = 0
  TheoreticalExact = false
  Type = 1
  UnderTolerance = 0
  X = 112.95
  Y = 14.3996
FEATURE [TechDraw::DrawViewBalloon] Balloon006
  BubbleShape = 0
  EndType = 0
  EndTypeScale = 1
  KinkLength = 5
  LockPosition = false
  OriginX = 8.99323
  OriginY = -13.3092
  Rotation = 0
  ScaleType = 0
  ShapeScale = 1
  SourceView = -> View005
  Text = 1
  TextWrapLen = -1
  X = 18.9932
  Y = -3.30923
FEATURE [TechDraw::DrawViewAnnotation] Annotation001
  Font = osifont
  LineSpace = 100
  LockPosition = false
  MaxWidth = -1
  Rotation = 0
  ScaleType = 0
  Text = 1: Agujeros sujección (6 x 3ø )
  TextSize = 5
  TextStyle = 0
  X = 207.271
  Y = 200.35
FEATURE [TechDraw::DrawViewDimension] Dimension059
  AngleOverride = false
  Arbitrary = false
  ArbitraryTolerances = false
  EqualTolerance = true
  ExtensionAngle = 0
  FormatSpec = %.2w
  FormatSpecOverTolerance = %+.2w
  FormatSpecUnderTolerance = %+.2w
  Inverted = false
  LineAngle = 0
  LockPosition = false
  MeasureType = 1
  OverTolerance = 0
  References2D = -> [View005]
  Rotation = 0
  ScaleType = 0
  TheoreticalExact = false
  Type = 1
  UnderTolerance = 0
  X = 22.4084
  Y = 84.5393
FEATURE [TechDraw::DrawViewDimension] Dimension060
  AngleOverride = false
  Arbitrary = false
  ArbitraryTolerances = false
  EqualTolerance = true
  ExtensionAngle = 0
  FormatSpec = %.2w
  FormatSpecOverTolerance = %+.2w
  FormatSpecUnderTolerance = %+.2w
  Inverted = false
  LineAngle = 0
  LockPosition = false
  MeasureType = 1
  OverTolerance = 0
  References2D = -> [View005]
  Rotation = 0
  ScaleType = 0
  TheoreticalExact = false
  Type = 1
  UnderTolerance = 0
  X = -37.879
  Y = 83.7054
FEATURE [TechDraw::DrawPage] Page  label="Planos-ardumega"
  KeepUpdated = true
  NextBalloonIndex = 2
  ProjectionType = 0
  Template = -> Template
  Views = -> [View004,View005,View006,View007,Dimension035,Dimension036,Dimension037,Dimension038,Dimension039,Dimension040,Dimension041,Dimension042,Dimension043,Dimension044,Dimension045,Dimension046,Dimension047,Dimension048,Dimension049,Dimension051,Dimension052,Dimension053,Dimension054,Dimension055,Dimension056,Dimension057,Dimension058,Balloon006,Annotation001,Dimension059,Dimension060]
FEATURE [Part::Refine] Compound008  label="pcb-support001"
  Source = -> Compound001
FEATURE [TechDraw::DrawSVGTemplate] Template003
  Height = 297
  Orientation = 1
  Template = <path>
  Width = 420
FEATURE [TechDraw::DrawViewPart] View009  label="Planta002"
  CoarseView = true
  Direction = (0,0,-1)
  Focus = 100
  HardHidden = false
  IsoCount = 0
  IsoHidden = false
  IsoVisible = false
  LockPosition = false
  Perspective = false
  Rotation = 0
  Scale = 2
  ScaleType = 2
  ScrubCount = 0
  SeamHidden = false
  SeamVisible = false
  SmoothHidden = false
  SmoothVisible = true
  Source = -> [Fusion001064]
  X = 75
  XDirection = (1,0,0)
  Y = 100
FEATURE [TechDraw::DrawViewPart] View010  label="Perfil002"
  CoarseView = true
  Direction = (-1,0,0)
  Focus = 100
  HardHidden = false
  IsoCount = 0
  IsoHidden = false
  IsoVisible = false
  LockPosition = false
  Perspective = false
  Rotation = 0
  Scale = 2
  ScaleType = 2
  ScrubCount = 0
  SeamHidden = false
  SeamVisible = false
  SmoothHidden = false
  SmoothVisible = true
  Source = -> [Fusion001064]
  X = 250
  XDirection = (0,-1,0)
  Y = 230
FEATURE [TechDraw::DrawViewPart] View011  label="Alzado002"
  CoarseView = true
  Direction = (0,-1,0)
  Focus = 100
  HardHidden = false
  IsoCount = 0
  IsoHidden = false
  IsoVisible = false
  LockPosition = false
  Perspective = false
  Rotation = 0
  Scale = 2
  ScaleType = 2
  ScrubCount = 0
  SeamHidden = false
  SeamVisible = false
  SmoothHidden = false
  SmoothVisible = true
  Source = -> [Fusion001064]
  X = 75
  XDirection = (1,0,0)
  Y = 230
FEATURE [TechDraw::DrawViewDimension] Dimension061
  AngleOverride = false
  Arbitrary = false
  ArbitraryTolerances = false
  EqualTolerance = true
  ExtensionAngle = 0
  FormatSpec = %.2w
  FormatSpecOverTolerance = %+.2w
  FormatSpecUnderTolerance = %+.2w
  Inverted = false
  LineAngle = 0
  LockPosition = false
  MeasureType = 1
  OverTolerance = 0
  References2D = -> [View011]
  Rotation = 0
  ScaleType = 0
  TheoreticalExact = false
  Type = 2
  UnderTolerance = 0
  X = -45.2214
  Y = -3.94814
FEATURE [TechDraw::DrawViewDimension] Dimension063
  AngleOverride = false
  Arbitrary = false
  ArbitraryTolerances = false
  EqualTolerance = true
  ExtensionAngle = 0
  FormatSpec = %.2w
  FormatSpecOverTolerance = %+.2w
  FormatSpecUnderTolerance = %+.2w
  Inverted = false
  LineAngle = 0
  LockPosition = false
  MeasureType = 1
  OverTolerance = 0
  References2D = -> [View011]
  Rotation = 0
  ScaleType = 0
  TheoreticalExact = false
  Type = 1
  UnderTolerance = 0
  X = -6.95433
  Y = 51.2276
FEATURE [TechDraw::DrawViewDimension] Dimension065
  AngleOverride = false
  Arbitrary = false
  ArbitraryTolerances = false
  EqualTolerance = true
  ExtensionAngle = 0
  FormatSpec = %.2w
  FormatSpecOverTolerance = %+.2w
  FormatSpecUnderTolerance = %+.2w
  Inverted = false
  LineAngle = 0
  LockPosition = false
  MeasureType = 1
  OverTolerance = 0
  References2D = -> [View011]
  Rotation = 0
  ScaleType = 0
  TheoreticalExact = false
  Type = 1
  UnderTolerance = 0
  X = 5
  Y = 11.8251
FEATURE [TechDraw::DrawViewDimension] Dimension066
  AngleOverride = false
  Arbitrary = false
  ArbitraryTolerances = false
  EqualTolerance = true
  ExtensionAngle = 0
  FormatSpec = %.2w
  FormatSpecOverTolerance = %+.2w
  FormatSpecUnderTolerance = %+.2w
  Inverted = false
  LineAngle = 0
  LockPosition = false
  MeasureType = 1
  OverTolerance = 0
  References2D = -> [View009]
  Rotation = 0
  ScaleType = 0
  TheoreticalExact = false
  Type = 1
  UnderTolerance = 0
  X = -18.8158
  Y = 83.6576
FEATURE [TechDraw::DrawViewDimension] Dimension067
  AngleOverride = false
  Arbitrary = false
  ArbitraryTolerances = false
  EqualTolerance = true
  ExtensionAngle = 0
  FormatSpec = %.2w
  FormatSpecOverTolerance = %+.2w
  FormatSpecUnderTolerance = %+.2w
  Inverted = false
  LineAngle = 0
  LockPosition = false
  MeasureType = 1
  OverTolerance = 0
  References2D = -> [View009]
  Rotation = 0
  ScaleType = 0
  TheoreticalExact = false
  Type = 2
  UnderTolerance = 0
  X = -42.5783
  Y = 6.31576
FEATURE [TechDraw::DrawViewDimension] Dimension068
  AngleOverride = false
  Arbitrary = false
  ArbitraryTolerances = false
  EqualTolerance = true
  ExtensionAngle = 0
  FormatSpec = %.2w
  FormatSpecOverTolerance = %+.2w
  FormatSpecUnderTolerance = %+.2w
  Inverted = false
  LineAngle = 0
  LockPosition = false
  MeasureType = 1
  OverTolerance = 0
  References2D = -> [View009]
  Rotation = 0
  ScaleType = 0
  TheoreticalExact = false
  Type = 2
  UnderTolerance = 0
  X = 35.9458
  Y = -1.9867
FEATURE [TechDraw::DrawViewDimension] Dimension069
  AngleOverride = false
  Arbitrary = false
  ArbitraryTolerances = false
  EqualTolerance = true
  ExtensionAngle = 0
  FormatSpec = %.2w
  FormatSpecOverTolerance = %+.2w
  FormatSpecUnderTolerance = %+.2w
  Inverted = false
  LineAngle = 0
  LockPosition = false
  MeasureType = 1
  OverTolerance = 0
  References2D = -> [View010]
  Rotation = 0
  ScaleType = 0
  TheoreticalExact = false
  Type = 1
  UnderTolerance = 0
  X = -0.368816
  Y = 33.1957
FEATURE [TechDraw::DrawViewDimension] Dimension070
  AngleOverride = false
  Arbitrary = false
  ArbitraryTolerances = false
  EqualTolerance = true
  ExtensionAngle = 0
  FormatSpec = %.2w
  FormatSpecOverTolerance = %+.2w
  FormatSpecUnderTolerance = %+.2w
  Inverted = false
  LineAngle = 0
  LockPosition = false
  MeasureType = 1
  OverTolerance = 0
  References2D = -> [View010]
  Rotation = 0
  ScaleType = 0
  TheoreticalExact = false
  Type = 1
  UnderTolerance = 0
  X = 0
  Y = 14.443
FEATURE [TechDraw::DrawViewDimension] Dimension071
  AngleOverride = false
  Arbitrary = false
  ArbitraryTolerances = false
  EqualTolerance = true
  ExtensionAngle = 0
  FormatSpec = %.2w
  FormatSpecOverTolerance = %+.2w
  FormatSpecUnderTolerance = %+.2w
  Inverted = false
  LineAngle = 0
  LockPosition = false
  MeasureType = 1
  OverTolerance = 0
  References2D = -> [View010]
  Rotation = 0
  ScaleType = 0
  TheoreticalExact = false
  Type = 2
  UnderTolerance = 0
  X = -62.4903
  Y = -0.606449
FEATURE [TechDraw::DrawViewDimension] Dimension072
  AngleOverride = false
  Arbitrary = false
  ArbitraryTolerances = false
  EqualTolerance = true
  ExtensionAngle = 0
  FormatSpec = %.2w
  FormatSpecOverTolerance = %+.2w
  FormatSpecUnderTolerance = %+.2w
  Inverted = false
  LineAngle = 0
  LockPosition = false
  MeasureType = 1
  OverTolerance = 0
  References2D = -> [View010]
  Rotation = 0
  ScaleType = 0
  TheoreticalExact = false
  Type = 2
  UnderTolerance = 0
  X = -54.8021
  Y = -0.975266
FEATURE [TechDraw::DrawViewDimension] Dimension073
  AngleOverride = false
  Arbitrary = false
  ArbitraryTolerances = false
  EqualTolerance = true
  ExtensionAngle = 0
  FormatSpec = %.2w
  FormatSpecOverTolerance = %+.2w
  FormatSpecUnderTolerance = %+.2w
  Inverted = false
  LineAngle = 0
  LockPosition = false
  MeasureType = 1
  OverTolerance = 0
  References2D = -> [View010]
  Rotation = 0
  ScaleType = 0
  TheoreticalExact = false
  Type = 2
  UnderTolerance = 0
  X = -94.0225
  Y = 0.287101
FEATURE [TechDraw::DrawViewDimension] Dimension074
  AngleOverride = false
  Arbitrary = false
  ArbitraryTolerances = false
  EqualTolerance = true
  ExtensionAngle = 0
  FormatSpec = %.2w
  FormatSpecOverTolerance = %+.2w
  FormatSpecUnderTolerance = %+.2w
  Inverted = false
  LineAngle = 0
  LockPosition = false
  MeasureType = 1
  OverTolerance = 0
  References2D = -> [View009]
  Rotation = 0
  ScaleType = 0
  TheoreticalExact = false
  Type = 1
  UnderTolerance = 0
  X = -33.2518
  Y = -72.4081
FEATURE [TechDraw::DrawViewPart] View012  label="Vista3D001"
  CoarseView = true
  Direction = (0.57735,-0.57735,0.57735)
  Focus = 100
  HardHidden = false
  IsoCount = 0
  IsoHidden = false
  IsoVisible = false
  LockPosition = false
  Perspective = false
  Rotation = 0
  Scale = 2
  ScaleType = 2
  ScrubCount = 0
  SeamHidden = false
  SeamVisible = false
  SmoothHidden = false
  SmoothVisible = true
  Source = -> [Fusion001064]
  X = 250
  XDirection = (0.707107,0.707107,0)
  Y = 120
FEATURE [TechDraw::DrawPage] Page003  label="Planos-Lipo"
  KeepUpdated = true
  NextBalloonIndex = 1
  ProjectionType = 0
  Template = -> Template003
  Views = -> [View009,View010,View011,Dimension061,Dimension063,Dimension065,Dimension066,Dimension067,Dimension068,Dimension069,Dimension070,Dimension071,Dimension072,Dimension073,Dimension074,View012]
FEATURE [TechDraw::DrawSVGTemplate] Template004
  Height = 297
  Orientation = 1
  Template = <path>
  Width = 420
FEATURE [TechDraw::DrawViewPart] View013
  CoarseView = true
  Direction = (0,-1,0)
  Focus = 100
  HardHidden = false
  IsoCount = 0
  IsoHidden = false
  IsoVisible = false
  LockPosition = false
  Perspective = false
  Rotation = 0
  Scale = 4
  ScaleType = 2
  ScrubCount = 0
  SeamHidden = false
  SeamVisible = false
  SmoothHidden = false
  SmoothVisible = true
  Source = -> [Compound008]
  X = 100.349
  XDirection = (1,0,0)
  Y = 95.5519
FEATURE [TechDraw::DrawViewPart] View014
  CoarseView = false
  Direction = (0,0,1)
  Focus = 100
  HardHidden = false
  IsoCount = 0
  IsoHidden = false
  IsoVisible = false
  LockPosition = false
  Perspective = false
  Rotation = 0
  ScaleType = 0
  ScrubCount = 0
  SeamHidden = false
  SeamVisible = false
  SmoothHidden = false
  SmoothVisible = true
  Source = -> [Compound008]
  X = 98.1269
  XDirection = (1,0,0)
  Y = 198.69
FEATURE [TechDraw::DrawViewPart] View015
  CoarseView = false
  Direction = (1,0,0)
  Focus = 100
  HardHidden = false
  IsoCount = 0
  IsoHidden = false
  IsoVisible = false
  LockPosition = false
  Perspective = false
  Rotation = 0
  ScaleType = 0
  ScrubCount = 0
  SeamHidden = false
  SeamVisible = false
  SmoothHidden = false
  SmoothVisible = true
  Source = -> [Compound008]
  X = 210
  XDirection = (0,1,0)
  Y = 148.5
FEATURE [TechDraw::DrawViewPart] View016
  CoarseView = false
  Direction = (0.57735,-0.57735,0.57735)
  Focus = 100
  HardHidden = false
  IsoCount = 0
  IsoHidden = false
  IsoVisible = false
  LockPosition = false
  Perspective = false
  Rotation = 0
  ScaleType = 0
  ScrubCount = 0
  SeamHidden = false
  SeamVisible = false
  SmoothHidden = false
  SmoothVisible = true
  Source = -> [Compound008]
  X = 210
  XDirection = (0.707107,0.707107,0)
  Y = 148.5
FEATURE [TechDraw::DrawPage] Page004  label="Planos-PDB"
  KeepUpdated = true
  NextBalloonIndex = 1
  ProjectionType = 0
  Template = -> Template004
  Views = -> [View013,View014,View015,View016]
FEATURE [App::DocumentObjectGroup] Group001  label="Componentes-interior"
  Group = -> [LinkGroup,Compound008,Box024]
FEATURE [App::DocumentObjectGroup] Group002  label="Tapa-Carcasa"
  Group = -> [Cut038]
FEATURE [App::DocumentObjectGroup] Group003  label="Carcasa-boceto-inicial"
  Group = -> [Body,YZ_Plane004]
FEATURE [Part::Feature] Compound009  label="carcasa-compound-simple"
  shape: bbox 165.6 x 170.1 x 47.45 mm, 385 faces, 3 solids (baked)
FEATURE [TechDraw::DrawViewPart] View  label="Alzado"
  CoarseView = true
  Direction = (0,-1,0)
  Focus = 100
  HardHidden = false
  IsoCount = 0
  IsoHidden = false
  IsoVisible = false
  LockPosition = true
  Perspective = false
  Rotation = 0
  ScaleType = 0
  ScrubCount = 0
  SeamHidden = false
  SeamVisible = false
  SmoothHidden = false
  SmoothVisible = true
  Source = -> [Compound009,Cut038]
  X = 110
  XDirection = (1,0,0)
  Y = 230
FEATURE [TechDraw::DrawViewPart] View017  label="Perfil"
  CoarseView = true
  Direction = (1,0,0)
  Focus = 100
  HardHidden = false
  IsoCount = 0
  IsoHidden = false
  IsoVisible = false
  LockPosition = true
  Perspective = false
  Rotation = 0
  ScaleType = 0
  ScrubCount = 0
  SeamHidden = false
  SeamVisible = false
  SmoothHidden = false
  SmoothVisible = true
  Source = -> [Cut038,Compound004]
  X = 300
  XDirection = (0,1,0)
  Y = 230
FEATURE [TechDraw::DrawViewDimension] Dimension
  AngleOverride = false
  Arbitrary = false
  ArbitraryTolerances = false
  EqualTolerance = true
  ExtensionAngle = 0
  FormatSpec = %.2w
  FormatSpecOverTolerance = %+.2w
  FormatSpecUnderTolerance = %+.2w
  Inverted = false
  LineAngle = 0
  LockPosition = false
  MeasureType = 1
  OverTolerance = 0
  References2D = -> [View]
  Rotation = 0
  ScaleType = 0
  TheoreticalExact = false
  Type = 1
  UnderTolerance = 0
  X = -0.773051
  Y = -14.0082
FEATURE [TechDraw::DrawViewDimension] Dimension075
  AngleOverride = false
  Arbitrary = false
  ArbitraryTolerances = false
  EqualTolerance = true
  ExtensionAngle = 0
  FormatSpec = %.2w
  FormatSpecOverTolerance = %+.2w
  FormatSpecUnderTolerance = %+.2w
  Inverted = false
  LineAngle = 0
  LockPosition = false
  MeasureType = 1
  OverTolerance = 0
  References2D = -> [View]
  Rotation = 0
  ScaleType = 0
  TheoreticalExact = false
  Type = 1
  UnderTolerance = 0
  X = -0.257684
  Y = -46.6726
FEATURE [TechDraw::DrawViewDimension] Dimension076
  AngleOverride = false
  Arbitrary = false
  ArbitraryTolerances = false
  EqualTolerance = true
  ExtensionAngle = 0
  FormatSpec = %.2w
  FormatSpecOverTolerance = %+.2w
  FormatSpecUnderTolerance = %+.2w
  Inverted = false
  LineAngle = 0
  LockPosition = false
  MeasureType = 1
  OverTolerance = 0
  References2D = -> [View]
  Rotation = 0
  ScaleType = 0
  TheoreticalExact = false
  Type = 1
  UnderTolerance = 0
  X = -1.03073
  Y = 46.5189
FEATURE [TechDraw::DrawViewDimension] Dimension077
  AngleOverride = false
  Arbitrary = false
  ArbitraryTolerances = false
  EqualTolerance = true
  ExtensionAngle = 0
  FormatSpec = %.2w
  FormatSpecOverTolerance = %+.2w
  FormatSpecUnderTolerance = %+.2w
  Inverted = false
  LineAngle = 0
  LockPosition = false
  MeasureType = 1
  OverTolerance = 0
  References2D = -> [View]
  Rotation = 0
  ScaleType = 0
  TheoreticalExact = false
  Type = 1
  UnderTolerance = 0
  X = -2.06147
  Y = 54.3109
FEATURE [TechDraw::DrawViewDimension] Dimension078
  AngleOverride = false
  Arbitrary = false
  ArbitraryTolerances = false
  EqualTolerance = true
  ExtensionAngle = 0
  FormatSpec = %.2w
  FormatSpecOverTolerance = %+.2w
  FormatSpecUnderTolerance = %+.2w
  Inverted = false
  LineAngle = 0
  LockPosition = false
  MeasureType = 1
  OverTolerance = 0
  References2D = -> [View]
  Rotation = 0
  ScaleType = 0
  TheoreticalExact = false
  Type = 0
  UnderTolerance = 0
  X = 85.5734
  Y = -24.8919
FEATURE [TechDraw::DrawViewDimension] Dimension079
  AngleOverride = false
  Arbitrary = false
  ArbitraryTolerances = false
  EqualTolerance = true
  ExtensionAngle = 0
  FormatSpec = %.2w
  FormatSpecOverTolerance = %+.2w
  FormatSpecUnderTolerance = %+.2w
  Inverted = false
  LineAngle = 0
  LockPosition = false
  MeasureType = 1
  OverTolerance = 0
  References2D = -> [View]
  Rotation = 0
  ScaleType = 0
  TheoreticalExact = false
  Type = 2
  UnderTolerance = 0
  X = 60
  Y = -25
FEATURE [TechDraw::DrawViewDimension] Dimension080
  AngleOverride = false
  Arbitrary = false
  ArbitraryTolerances = false
  EqualTolerance = true
  ExtensionAngle = 0
  FormatSpec = %.2w
  FormatSpecOverTolerance = %+.2w
  FormatSpecUnderTolerance = %+.2w
  Inverted = false
  LineAngle = 0
  LockPosition = false
  MeasureType = 1
  OverTolerance = 0
  References2D = -> [View]
  Rotation = 0
  ScaleType = 0
  TheoreticalExact = false
  Type = 2
  UnderTolerance = 0
  X = -70.6147
  Y = -28.7423
FEATURE [TechDraw::DrawViewDimension] Dimension081
  AngleOverride = false
  Arbitrary = false
  ArbitraryTolerances = false
  EqualTolerance = true
  ExtensionAngle = 0
  FormatSpec = %.2w
  FormatSpecOverTolerance = %+.2w
  FormatSpecUnderTolerance = %+.2w
  Inverted = false
  LineAngle = 0
  LockPosition = false
  MeasureType = 1
  OverTolerance = 0
  References2D = -> [View]
  Rotation = 0
  ScaleType = 0
  TheoreticalExact = false
  Type = 1
  UnderTolerance = 0
  X = 55
  Y = -36.2612
FEATURE [TechDraw::DrawViewDimension] Dimension082
  AngleOverride = false
  Arbitrary = false
  ArbitraryTolerances = false
  EqualTolerance = true
  ExtensionAngle = 0
  FormatSpec = %.2w
  FormatSpecOverTolerance = %+.2w
  FormatSpecUnderTolerance = %+.2w
  Inverted = false
  LineAngle = 0
  LockPosition = false
  MeasureType = 1
  OverTolerance = 0
  References2D = -> [View]
  Rotation = 0
  ScaleType = 0
  TheoreticalExact = false
  Type = 0
  UnderTolerance = 0
  X = 77.6373
  Y = -4.12379
FEATURE [TechDraw::DrawViewDimension] Dimension083
  AngleOverride = false
  Arbitrary = false
  ArbitraryTolerances = false
  EqualTolerance = true
  ExtensionAngle = 0
  FormatSpec = %.2w
  FormatSpecOverTolerance = %+.2w
  FormatSpecUnderTolerance = %+.2w
  Inverted = false
  LineAngle = 0
  LockPosition = false
  MeasureType = 1
  OverTolerance = 0
  References2D = -> [View]
  Rotation = 0
  ScaleType = 0
  TheoreticalExact = false
  Type = 2
  UnderTolerance = 0
  X = -92.0024
  Y = 0.268051
FEATURE [TechDraw::DrawViewDimension] Dimension084
  AngleOverride = false
  Arbitrary = false
  ArbitraryTolerances = false
  EqualTolerance = true
  ExtensionAngle = 0
  FormatSpec = %.2w
  FormatSpecOverTolerance = %+.2w
  FormatSpecUnderTolerance = %+.2w
  Inverted = false
  LineAngle = 0
  LockPosition = false
  MeasureType = 1
  OverTolerance = 0
  References2D = -> [View]
  Rotation = 0
  ScaleType = 0
  TheoreticalExact = false
  Type = 2
  UnderTolerance = 0
  X = -92.0024
  Y = -20.5204
FEATURE [TechDraw::DrawViewDimension] Dimension085
  AngleOverride = false
  Arbitrary = false
  ArbitraryTolerances = false
  EqualTolerance = true
  ExtensionAngle = 0
  FormatSpec = %.2w
  FormatSpecOverTolerance = %+.2w
  FormatSpecUnderTolerance = %+.2w
  Inverted = false
  LineAngle = 0
  LockPosition = false
  MeasureType = 1
  OverTolerance = 0
  References2D = -> [View017]
  Rotation = 0
  ScaleType = 0
  TheoreticalExact = false
  Type = 2
  UnderTolerance = 0
  X = -96.1262
  Y = 24
FEATURE [TechDraw::DrawViewDimension] Dimension086
  AngleOverride = false
  Arbitrary = false
  ArbitraryTolerances = false
  EqualTolerance = true
  ExtensionAngle = 0
  FormatSpec = %.2w
  FormatSpecOverTolerance = %+.2w
  FormatSpecUnderTolerance = %+.2w
  Inverted = false
  LineAngle = 0
  LockPosition = false
  MeasureType = 1
  OverTolerance = 0
  References2D = -> [View017]
  Rotation = 0
  ScaleType = 0
  TheoreticalExact = false
  Type = 2
  UnderTolerance = 0
  X = -100.836
  Y = 40.0354
FEATURE [TechDraw::DrawViewDimension] Dimension087
  AngleOverride = false
  Arbitrary = false
  ArbitraryTolerances = false
  EqualTolerance = true
  ExtensionAngle = 0
  FormatSpec = %.2w
  FormatSpecOverTolerance = %+.2w
  FormatSpecUnderTolerance = %+.2w
  Inverted = false
  LineAngle = 0
  LockPosition = false
  MeasureType = 1
  OverTolerance = 0
  References2D = -> [View017]
  Rotation = 0
  ScaleType = 0
  TheoreticalExact = false
  Type = 2
  UnderTolerance = 0
  X = -92.1588
  Y = 7.96127
FEATURE [TechDraw::DrawViewDimension] Dimension088
  AngleOverride = false
  Arbitrary = false
  ArbitraryTolerances = false
  EqualTolerance = true
  ExtensionAngle = 0
  FormatSpec = %.2w
  FormatSpecOverTolerance = %+.2w
  FormatSpecUnderTolerance = %+.2w
  Inverted = false
  LineAngle = 0
  LockPosition = false
  MeasureType = 1
  OverTolerance = 0
  References2D = -> [View017]
  Rotation = 0
  ScaleType = 0
  TheoreticalExact = false
  Type = 1
  UnderTolerance = 0
  X = 10.278
  Y = 22.4024
FEATURE [TechDraw::DrawViewDimension] Dimension089
  AngleOverride = false
  Arbitrary = false
  ArbitraryTolerances = false
  EqualTolerance = true
  ExtensionAngle = 0
  FormatSpec = %.2w
  FormatSpecOverTolerance = %+.2w
  FormatSpecUnderTolerance = %+.2w
  Inverted = false
  LineAngle = 0
  LockPosition = false
  MeasureType = 1
  OverTolerance = 0
  References2D = -> [View017]
  Rotation = 0
  ScaleType = 0
  TheoreticalExact = false
  Type = 2
  UnderTolerance = 0
  X = -8.74612
  Y = 5.65534
FEATURE [TechDraw::DrawViewDimension] Dimension090
  AngleOverride = false
  Arbitrary = false
  ArbitraryTolerances = false
  EqualTolerance = true
  ExtensionAngle = 0
  FormatSpec = %.2w
  FormatSpecOverTolerance = %+.2w
  FormatSpecUnderTolerance = %+.2w
  Inverted = false
  LineAngle = 0
  LockPosition = false
  MeasureType = 1
  OverTolerance = 0
  References2D = -> [View017]
  Rotation = 0
  ScaleType = 0
  TheoreticalExact = false
  Type = 1
  UnderTolerance = 0
  X = 31.9872
  Y = -16.7489
FEATURE [TechDraw::DrawViewDimension] Dimension091
  AngleOverride = false
  Arbitrary = false
  ArbitraryTolerances = false
  EqualTolerance = true
  ExtensionAngle = 0
  FormatSpec = %.2w
  FormatSpecOverTolerance = %+.2w
  FormatSpecUnderTolerance = %+.2w
  Inverted = false
  LineAngle = 0
  LockPosition = false
  MeasureType = 1
  OverTolerance = 0
  References2D = -> [View017]
  Rotation = 0
  ScaleType = 0
  TheoreticalExact = false
  Type = 1
  UnderTolerance = 0
  X = -75.0473
  Y = -22.5
FEATURE [TechDraw::DrawViewDimension] Dimension092
  AngleOverride = false
  Arbitrary = false
  ArbitraryTolerances = false
  EqualTolerance = true
  ExtensionAngle = 0
  FormatSpec = %.2w
  FormatSpecOverTolerance = %+.2w
  FormatSpecUnderTolerance = %+.2w
  Inverted = false
  LineAngle = 0
  LockPosition = false
  MeasureType = 1
  OverTolerance = 0
  References2D = -> [View017]
  Rotation = 0
  ScaleType = 0
  TheoreticalExact = false
  Type = 1
  UnderTolerance = 0
  X = -0.290025
  Y = -35.898
FEATURE [TechDraw::DrawViewBalloon] Balloon007
  BubbleShape = 0
  EndType = 0
  EndTypeScale = 1
  KinkLength = 5
  LockPosition = false
  OriginX = 54.139
  OriginY = -10.1604
  Rotation = 0
  ScaleType = 0
  ShapeScale = 1
  SourceView = -> View
  Text = 1
  TextWrapLen = -1
  X = 74.139
  Y = 9.83958
FEATURE [TechDraw::DrawViewBalloon] Balloon008
  BubbleShape = 0
  EndType = 0
  EndTypeScale = 1
  KinkLength = 5
  LockPosition = false
  OriginX = -53.7068
  OriginY = -27.3446
  Rotation = 0
  ScaleType = 0
  ShapeScale = 1
  SourceView = -> View
  Text = 2
  TextWrapLen = -1
  X = -74.0009
  Y = 22.8759
FEATURE [TechDraw::DrawViewBalloon] Balloon009
  BubbleShape = 0
  EndType = 0
  EndTypeScale = 1
  KinkLength = 5
  LockPosition = false
  OriginX = 11.5053
  OriginY = -0.794683
  Rotation = 0
  ScaleType = 0
  ShapeScale = 1
  SourceView = -> Dimension092
  Text = 3
  TextWrapLen = -1
  X = 50.4342
  Y = 18.3823
FEATURE [TechDraw::DrawViewPart] View019  label="Planta"
  CoarseView = true
  Direction = (0,0,-1)
  Focus = 100
  HardHidden = false
  IsoCount = 0
  IsoHidden = false
  IsoVisible = false
  LockPosition = true
  Perspective = false
  Rotation = 0
  ScaleType = 0
  ScrubCount = 0
  SeamHidden = false
  SeamVisible = false
  SmoothHidden = false
  SmoothVisible = true
  Source = -> [Compound009]
  X = 110
  XDirection = (1,0,0)
  Y = 100
FEATURE [TechDraw::DrawViewDimension] Dimension093
  AngleOverride = false
  Arbitrary = false
  ArbitraryTolerances = false
  EqualTolerance = true
  ExtensionAngle = 0
  FormatSpec = %.2w
  FormatSpecOverTolerance = %+.2w
  FormatSpecUnderTolerance = %+.2w
  Inverted = false
  LineAngle = 0
  LockPosition = false
  MeasureType = 1
  OverTolerance = 0
  References2D = -> [View019]
  Rotation = 0
  ScaleType = 0
  TheoreticalExact = false
  Type = 2
  UnderTolerance = 0
  X = 101.151
  Y = 1.33664
FEATURE [TechDraw::DrawViewDimension] Dimension094
  AngleOverride = false
  Arbitrary = false
  ArbitraryTolerances = false
  EqualTolerance = true
  ExtensionAngle = 0
  FormatSpec = %.2w
  FormatSpecOverTolerance = %+.2w
  FormatSpecUnderTolerance = %+.2w
  Inverted = false
  LineAngle = 0
  LockPosition = false
  MeasureType = 1
  OverTolerance = 0
  References2D = -> [View019]
  Rotation = 0
  ScaleType = 0
  TheoreticalExact = false
  Type = 2
  UnderTolerance = 0
  X = -87.6109
  Y = 6.91198
FEATURE [TechDraw::DrawViewDimension] Dimension095
  AngleOverride = false
  Arbitrary = false
  ArbitraryTolerances = false
  EqualTolerance = true
  ExtensionAngle = 0
  FormatSpec = %.2w
  FormatSpecOverTolerance = %+.2w
  FormatSpecUnderTolerance = %+.2w
  Inverted = false
  LineAngle = 0
  LockPosition = false
  MeasureType = 1
  OverTolerance = 0
  References2D = -> [View019]
  Rotation = 0
  ScaleType = 0
  TheoreticalExact = false
  Type = 2
  UnderTolerance = 0
  X = 65.6531
  Y = -79.7422
FEATURE [TechDraw::DrawViewDimension] Dimension097
  AngleOverride = false
  Arbitrary = false
  ArbitraryTolerances = false
  EqualTolerance = true
  ExtensionAngle = 0
  FormatSpec = %.2w
  FormatSpecOverTolerance = %+.2w
  FormatSpecUnderTolerance = %+.2w
  Inverted = false
  LineAngle = 0
  LockPosition = false
  MeasureType = 1
  OverTolerance = 0
  References2D = -> [View019]
  Rotation = 0
  ScaleType = 0
  TheoreticalExact = false
  Type = 2
  UnderTolerance = 0
  X = -70.2282
  Y = 4.45986
FEATURE [TechDraw::DrawViewDimension] Dimension098
  AngleOverride = false
  Arbitrary = false
  ArbitraryTolerances = false
  EqualTolerance = true
  ExtensionAngle = 0
  FormatSpec = %.2w
  FormatSpecOverTolerance = %+.2w
  FormatSpecUnderTolerance = %+.2w
  Inverted = false
  LineAngle = 0
  LockPosition = false
  MeasureType = 1
  OverTolerance = 0
  References2D = -> [View019]
  Rotation = 0
  ScaleType = 0
  TheoreticalExact = false
  Type = 2
  UnderTolerance = 0
  X = -69.4845
  Y = -72.2419
FEATURE [TechDraw::DrawViewDimension] Dimension099
  AngleOverride = false
  Arbitrary = false
  ArbitraryTolerances = false
  EqualTolerance = true
  ExtensionAngle = 0
  FormatSpec = %.2w
  FormatSpecOverTolerance = %+.2w
  FormatSpecUnderTolerance = %+.2w
  Inverted = false
  LineAngle = 0
  LockPosition = false
  MeasureType = 1
  OverTolerance = 0
  References2D = -> [View019]
  Rotation = 0
  ScaleType = 0
  TheoreticalExact = false
  Type = 1
  UnderTolerance = 0
  X = -66.052
  Y = -51.0713
FEATURE [TechDraw::DrawViewBalloon] Balloon010
  BubbleShape = 0
  EndType = 0
  EndTypeScale = 1
  KinkLength = 5
  LockPosition = false
  OriginX = 66.187
  OriginY = 5.3829
  Rotation = 0
  ScaleType = 0
  ShapeScale = 1
  SourceView = -> View019
  Text = 3
  TextWrapLen = -1
  X = 84.5404
  Y = 38.5558
FEATURE [TechDraw::DrawViewBalloon] Balloon011
  BubbleShape = 0
  EndType = 0
  EndTypeScale = 1
  KinkLength = 5
  LockPosition = false
  OriginX = -55.0033
  OriginY = -75.9595
  Rotation = 0
  ScaleType = 0
  ShapeScale = 1
  SourceView = -> View019
  Text = 0,3⌀
  TextWrapLen = -1
  X = -35.0033
  Y = -55.9595
FEATURE [TechDraw::DrawPage] Page002  label="Planos"
  KeepUpdated = true
  NextBalloonIndex = 17
  ProjectionType = 0
  Template = -> Template002
  Views = -> [Annotation,View003,Dimension030,Dimension031,Dimension032,Dimension033,Balloon,Balloon001,Balloon004,View,View017,Dimension,Dimension075,Dimension076,Dimension077,Dimension078,Dimension079,Dimension080,Dimension081,Dimension082,Dimension083,Dimension084,Dimension085,Dimension086,Dimension087,Dimension088,Dimension089,Dimension090,Dimension091,Dimension092,Balloon007,Balloon008,Balloon009,View019,+8 more]
FEATURE [TechDraw::DrawViewAnnotation] Annotation002
  Font = osifont
  LineSpace = 100
  LockPosition = false
  MaxWidth = -1
  Rotation = 0
  ScaleType = 0
  Text = 1: Tanque de flotación izquierdo | 2: Tanque de flotación central | 3: Tanque de flotación derecho
  TextSize = 5
  TextStyle = 0
  X = 218.568
  Y = 151.764
FEATURE [Part::Box] Box032  label="flotadores"
  AttacherType = Attacher::AttachEngine3D
  Height = 5
  Length = 10
  Placement = pos=(-60,-85,0) rot=(0,0,1;0rad)
  Width = 20
FEATURE [Part::Box] Box033  label="Cube006"
  AttacherType = Attacher::AttachEngine3D
  Height = 20
  Length = 50
  Placement = pos=(-62,-97,-15) rot=(0,0,1;0rad)
  Width = 30
FEATURE [Part::Box] Box034  label="Cube007"
  AttacherType = Attacher::AttachEngine3D
  Height = 16
  Length = 2
  Placement = pos=(-52,-77.5,-15) rot=(0,0,1;0rad)
  Width = 5
FEATURE [Part::Box] Box035  label="Cube008"
  AttacherType = Attacher::AttachEngine3D
  Height = 20
  Length = 50
  Placement = pos=(-62,-97,-15) rot=(0,0,1;0rad)
  Width = 30
FEATURE [Part::Box] Box036  label="Cube009"
  AttacherType = Attacher::AttachEngine3D
  Height = 5
  Length = 5
  Placement = pos=(15,-77.5,-20) rot=(0,0,1;0rad)
  Width = 5
FEATURE [Part::Cylinder] Cylinder009  label="tanques"
  Angle = 360
  AttacherType = Attacher::AttachEngine3D
  FirstAngle = 0
  Height = 220
  Placement = pos=(-35,-110,-15) rot=(0.57735,-0.57735,-0.57735;4.18879rad)
  Radius = 15
  SecondAngle = 0
FEATURE [Part::Cylinder] Cylinder010  label="tanques001"
  Angle = 360
  AttacherType = Attacher::AttachEngine3D
  FirstAngle = 0
  Height = 220
  Placement = pos=(-35,-110,-15) rot=(0.57735,-0.57735,-0.57735;4.18879rad)
  Radius = 15
  SecondAngle = 0
FEATURE [Part::Cylinder] Cylinder011  label="tanques002"
  Angle = 360
  AttacherType = Attacher::AttachEngine3D
  FirstAngle = 0
  Height = 220
  Placement = pos=(-35,-110,-15) rot=(0.57735,-0.57735,-0.57735;4.18879rad)
  Radius = 15
  SecondAngle = 0
FEATURE [Part::Fillet] Fillet002  label="tanque"
  Base = -> Cylinder009
  Edges = 2 edges r=5: [Edge2,Edge3]
FEATURE [Part::Fillet] Fillet003  label="tanque001"
  Base = -> Cylinder010
  Edges = 2 edges r=5: [Edge2,Edge3]
  Placement = pos=(35,0,0) rot=(0,0,1;0rad)
FEATURE [Part::Fillet] Fillet004  label="tanque002"
  Base = -> Cylinder011
  Edges = 2 edges r=5: [Edge2,Edge3]
  Placement = pos=(70,0,0) rot=(0,0,1;0rad)
FEATURE [Part::Feature] Fusion001067  label="Rosca macho020"
  Placement = pos=(-55,-75,-5) rot=(0,0,1;0rad)
  shape: bbox 3.919 x 4.387 x 44 mm, 35 faces (baked)
FEATURE [App::DocumentObjectGroup] Group004  label="tanques_conjunto"
  Group = -> [Fillet002,Fillet003,Fillet004]
FEATURE [Part::Mirroring] Part__Mirroring030  label="Cube009 (Mirror #13)"
  Base = (0,0,0)
  Normal = (1,0,0)
  Source = -> Box036
FEATURE [Part::Fuse] Fusion001069
  Base = -> Box036
  Refine = true
  Tool = -> Part__Mirroring030
FEATURE [TechDraw::DrawSVGTemplate] Template005
  Height = 297
  Orientation = 1
  Template = <path>
  Width = 420
FEATURE [Part::FeaturePython] Tube  # WARN: FeaturePython — macro-defined, semantics opaque (R4)
  AttacherType = Attacher::AttachEngine3D
  Height = 5
  InnerRadius = 15
  OuterRadius = 17
  Placement = pos=(-35,-77.5,-15) rot=(0.57735,-0.57735,-0.57735;4.18879rad)
FEATURE [Part::Cut] Cut044
  Base = -> Tube
  Refine = true
  Tool = -> Box033
FEATURE [Part::Fuse] Fusion001065
  Base = -> Cut044
  Refine = true
  Tool = -> Box034
FEATURE [Part::Fuse] Fusion001066  label="Flotador"
  Base = -> Box032
  Refine = true
  Tool = -> Fusion001065
FEATURE [Part::Cut] Cut046  label="flotadores001"
  Base = -> Fusion001066
  Refine = true
  Tool = -> Fusion001067
FEATURE [Part::Mirroring] Part__Mirroring028  label="flotadores001 (Mirror #11)"
  Base = (0,0,0)
  Normal = (1,0,0)
  Source = -> Cut046
FEATURE [Part::Fuse] Fusion001068
  Base = -> Cut046
  Refine = true
  Tool = -> Part__Mirroring028
FEATURE [Part::FeaturePython] Tube002  # WARN: FeaturePython — macro-defined, semantics opaque (R4)
  AttacherType = Attacher::AttachEngine3D
  Height = 5
  InnerRadius = 15
  OuterRadius = 17
  Placement = pos=(-35,-77.5,-15) rot=(0.57735,-0.57735,-0.57735;4.18879rad)
FEATURE [Part::Cut] Cut045
  Base = -> Tube002
  Placement = pos=(35,0,0) rot=(0,0,1;0rad)
  Refine = true
  Tool = -> Box035
FEATURE [Part::Fuse] Fusion001070
  Base = -> Cut045
  Refine = true
  Tool = -> Fusion001069
FEATURE [Part::Fuse] Fusion001071  label="sujecion-flotadores"
  Base = -> Fusion001068
  Refine = true
  Tool = -> Fusion001070
FEATURE [Part::Mirroring] Part__Mirroring031  label="sujecion-flotadores (Mirror #13)"
  Base = (0,0,0)
  Normal = (0,1,0)
  Source = -> Fusion001071
FEATURE [TechDraw::DrawViewPart] View020  label="Alzado003"
  CoarseView = true
  Direction = (0,-1,0)
  Focus = 100
  HardHidden = false
  IsoCount = 0
  IsoHidden = false
  IsoVisible = false
  LockPosition = true
  Perspective = false
  Rotation = 0
  ScaleType = 0
  ScrubCount = 0
  SeamHidden = false
  SeamVisible = false
  SmoothHidden = false
  SmoothVisible = true
  Source = -> [Fusion001071]
  X = 110
  XDirection = (1,0,0)
  Y = 230
FEATURE [TechDraw::DrawViewDimension] Dimension100
  AngleOverride = false
  Arbitrary = false
  ArbitraryTolerances = false
  EqualTolerance = true
  ExtensionAngle = 0
  FormatSpec = %.2w
  FormatSpecOverTolerance = %+.2w
  FormatSpecUnderTolerance = %+.2w
  Inverted = false
  LineAngle = 0
  LockPosition = false
  MeasureType = 1
  OverTolerance = 0
  References2D = -> [View020]
  Rotation = 0
  ScaleType = 0
  TheoreticalExact = false
  Type = 1
  UnderTolerance = 0
  X = -17.141
  Y = 9.61539
FEATURE [TechDraw::DrawViewDimension] Dimension001
  AngleOverride = false
  Arbitrary = false
  ArbitraryTolerances = false
  EqualTolerance = true
  ExtensionAngle = 0
  FormatSpec = %.2w
  FormatSpecOverTolerance = %+.2w
  FormatSpecUnderTolerance = %+.2w
  Inverted = false
  LineAngle = 0
  LockPosition = false
  MeasureType = 1
  OverTolerance = 0
  References2D = -> [View020]
  Rotation = 0
  ScaleType = 0
  TheoreticalExact = false
  Type = 1
  UnderTolerance = 0
  X = -18.2376
  Y = -16.7856
FEATURE [TechDraw::DrawViewDimension] Dimension004
  AngleOverride = false
  Arbitrary = false
  ArbitraryTolerances = false
  EqualTolerance = true
  ExtensionAngle = 0
  FormatSpec = %.2w
  FormatSpecOverTolerance = %+.2w
  FormatSpecUnderTolerance = %+.2w
  Inverted = false
  LineAngle = 0
  LockPosition = false
  MeasureType = 1
  OverTolerance = 0
  References2D = -> [View020]
  Rotation = 0
  ScaleType = 0
  TheoreticalExact = false
  Type = 2
  UnderTolerance = 0
  X = -81.2594
  Y = 6.53298
FEATURE [TechDraw::DrawViewDimension] Dimension007
  AngleOverride = false
  Arbitrary = false
  ArbitraryTolerances = false
  EqualTolerance = true
  ExtensionAngle = 0
  FormatSpec = %.2w
  FormatSpecOverTolerance = %+.2w
  FormatSpecUnderTolerance = %+.2w
  Inverted = false
  LineAngle = 0
  LockPosition = false
  MeasureType = 1
  OverTolerance = 0
  References2D = -> [View020]
  Rotation = 0
  ScaleType = 0
  TheoreticalExact = false
  Type = 1
  UnderTolerance = 0
  X = -46.8719
  Y = 12.4911
FEATURE [TechDraw::DrawViewDimension] Dimension010
  AngleOverride = false
  Arbitrary = false
  ArbitraryTolerances = false
  EqualTolerance = true
  ExtensionAngle = 0
  FormatSpec = %.2w
  FormatSpecOverTolerance = %+.2w
  FormatSpecUnderTolerance = %+.2w
  Inverted = false
  LineAngle = 0
  LockPosition = false
  MeasureType = 1
  OverTolerance = 0
  References2D = -> [View020]
  Rotation = 0
  ScaleType = 0
  TheoreticalExact = false
  Type = 2
  UnderTolerance = 0
  X = 27.6975
  Y = -1.04706
FEATURE [TechDraw::DrawViewPart] View001  label="Planta003"
  CoarseView = true
  Direction = (0,0,1)
  Focus = 100
  HardHidden = false
  IsoCount = 0
  IsoHidden = false
  IsoVisible = false
  LockPosition = true
  Perspective = false
  Rotation = 0
  ScaleType = 0
  ScrubCount = 0
  SeamHidden = false
  SeamVisible = false
  SmoothHidden = false
  SmoothVisible = true
  Source = -> [Fusion001071]
  X = 110
  XDirection = (1,0,0)
  Y = 80
FEATURE [TechDraw::DrawViewDimension] Dimension008
  AngleOverride = false
  Arbitrary = false
  ArbitraryTolerances = false
  EqualTolerance = true
  ExtensionAngle = 0
  FormatSpec = %.2w
  FormatSpecOverTolerance = %+.2w
  FormatSpecUnderTolerance = %+.2w
  Inverted = false
  LineAngle = 0
  LockPosition = false
  MeasureType = 1
  OverTolerance = 0
  References2D = -> [View001]
  Rotation = 0
  ScaleType = 0
  TheoreticalExact = false
  Type = 1
  UnderTolerance = 0
  X = -56.0769
  Y = 26.141
FEATURE [TechDraw::DrawViewDimension] Dimension009
  AngleOverride = false
  Arbitrary = false
  ArbitraryTolerances = false
  EqualTolerance = true
  ExtensionAngle = 0
  FormatSpec = %.2w
  FormatSpecOverTolerance = %+.2w
  FormatSpecUnderTolerance = %+.2w
  Inverted = false
  LineAngle = 0
  LockPosition = false
  MeasureType = 1
  OverTolerance = 0
  References2D = -> [View001]
  Rotation = 0
  ScaleType = 0
  TheoreticalExact = false
  Type = 2
  UnderTolerance = 0
  X = 67.8974
  Y = 2.14102
FEATURE [TechDraw::DrawViewDimension] Dimension012
  AngleOverride = false
  Arbitrary = false
  ArbitraryTolerances = false
  EqualTolerance = true
  ExtensionAngle = 0
  FormatSpec = %.2w
  FormatSpecOverTolerance = %+.2w
  FormatSpecUnderTolerance = %+.2w
  Inverted = false
  LineAngle = 0
  LockPosition = false
  MeasureType = 1
  OverTolerance = 0
  References2D = -> [View001]
  Rotation = 0
  ScaleType = 0
  TheoreticalExact = false
  Type = 1
  UnderTolerance = 0
  X = -32.7858
  Y = 48.7119
FEATURE [TechDraw::DrawViewDimension] Dimension013
  AngleOverride = false
  Arbitrary = false
  ArbitraryTolerances = false
  EqualTolerance = true
  ExtensionAngle = 0
  FormatSpec = %.2w
  FormatSpecOverTolerance = %+.2w
  FormatSpecUnderTolerance = %+.2w
  Inverted = false
  LineAngle = 0
  LockPosition = false
  MeasureType = 1
  OverTolerance = 0
  References2D = -> [View001]
  Rotation = 0
  ScaleType = 0
  TheoreticalExact = false
  Type = 1
  UnderTolerance = 0
  X = -0.170321
  Y = 48.5416
FEATURE [TechDraw::DrawViewDimension] Dimension014
  AngleOverride = false
  Arbitrary = false
  ArbitraryTolerances = false
  EqualTolerance = true
  ExtensionAngle = 0
  FormatSpec = %.2w
  FormatSpecOverTolerance = %+.2w
  FormatSpecUnderTolerance = %+.2w
  Inverted = false
  LineAngle = 0
  LockPosition = false
  MeasureType = 1
  OverTolerance = 0
  References2D = -> [View001]
  Rotation = 0
  ScaleType = 0
  TheoreticalExact = false
  Type = 1
  UnderTolerance = 0
  X = 32.9561
  Y = 48.8822
FEATURE [TechDraw::DrawViewDimension] Dimension015
  AngleOverride = false
  Arbitrary = false
  ArbitraryTolerances = false
  EqualTolerance = true
  ExtensionAngle = 0
  FormatSpec = %.2w
  FormatSpecOverTolerance = %+.2w
  FormatSpecUnderTolerance = %+.2w
  Inverted = false
  LineAngle = 0
  LockPosition = false
  MeasureType = 1
  OverTolerance = 0
  References2D = -> [View001]
  Rotation = 0
  ScaleType = 0
  TheoreticalExact = false
  Type = 1
  UnderTolerance = 0
  X = -1.06451
  Y = -24.7983
FEATURE [TechDraw::DrawViewPart] View002  label="Perfil003"
  CoarseView = true
  Direction = (1,0,0)
  Focus = 100
  HardHidden = false
  IsoCount = 0
  IsoHidden = false
  IsoVisible = false
  LockPosition = true
  Perspective = false
  Rotation = 0
  ScaleType = 0
  ScrubCount = 0
  SeamHidden = false
  SeamVisible = false
  SmoothHidden = false
  SmoothVisible = true
  Source = -> [Fusion001071]
  X = 320
  XDirection = (0,1,0)
  Y = 230
FEATURE [TechDraw::DrawViewDimension] Dimension003
  AngleOverride = false
  Arbitrary = false
  ArbitraryTolerances = false
  EqualTolerance = true
  ExtensionAngle = 0
  FormatSpec = %.2w
  FormatSpecOverTolerance = %+.2w
  FormatSpecUnderTolerance = %+.2w
  Inverted = false
  LineAngle = 0
  LockPosition = false
  MeasureType = 1
  OverTolerance = 0
  References2D = -> [View002]
  Rotation = 0
  ScaleType = 0
  TheoreticalExact = false
  Type = 1
  UnderTolerance = 0
  X = -0.678581
  Y = -33.2458
FEATURE [TechDraw::DrawViewDimension] Dimension005
  AngleOverride = false
  Arbitrary = false
  ArbitraryTolerances = false
  EqualTolerance = true
  ExtensionAngle = 0
  FormatSpec = %.2w
  FormatSpecOverTolerance = %+.2w
  FormatSpecUnderTolerance = %+.2w
  Inverted = false
  LineAngle = 0
  LockPosition = false
  MeasureType = 1
  OverTolerance = 0
  References2D = -> [View002]
  Rotation = 0
  ScaleType = 0
  TheoreticalExact = false
  Type = 2
  UnderTolerance = 0
  X = -42.4558
  Y = 17.7624
FEATURE [TechDraw::DrawViewDimension] Dimension011
  AngleOverride = false
  Arbitrary = false
  ArbitraryTolerances = false
  EqualTolerance = true
  ExtensionAngle = 0
  FormatSpec = %.2w
  FormatSpecOverTolerance = %+.2w
  FormatSpecUnderTolerance = %+.2w
  Inverted = false
  LineAngle = 0
  LockPosition = false
  MeasureType = 1
  OverTolerance = 0
  References2D = -> [View002]
  Rotation = 0
  ScaleType = 0
  TheoreticalExact = false
  Type = 1
  UnderTolerance = 0
  X = -5.76779
  Y = 29.3812
FEATURE [TechDraw::DrawViewPart] View021  label="3DView"
  CoarseView = true
  Direction = (0.57735,-0.57735,0.57735)
  Focus = 100
  HardHidden = false
  IsoCount = 0
  IsoHidden = false
  IsoVisible = false
  LockPosition = true
  Perspective = false
  Rotation = 0
  ScaleType = 0
  ScrubCount = 0
  SeamHidden = false
  SeamVisible = false
  SmoothHidden = false
  SmoothVisible = true
  Source = -> [Fusion001071]
  X = 320
  XDirection = (0.707107,0.707107,0)
  Y = 130
FEATURE [TechDraw::DrawViewBalloon] Balloon012
  BubbleShape = 0
  EndType = 0
  EndTypeScale = 1
  KinkLength = 5
  LockPosition = false
  OriginX = -21.8546
  OriginY = 9.71666
  Rotation = 0
  ScaleType = 0
  ShapeScale = 1
  SourceView = -> View021
  Text = 1
  TextWrapLen = -1
  X = -1.85463
  Y = 29.7167
FEATURE [TechDraw::DrawViewBalloon] Balloon013
  BubbleShape = 0
  EndType = 0
  EndTypeScale = 1
  KinkLength = 5
  LockPosition = false
  OriginX = 2.60604
  OriginY = -9.07914
  Rotation = 0
  ScaleType = 0
  ShapeScale = 1
  SourceView = -> View021
  Text = 2
  TextWrapLen = -1
  X = 21.3821
  Y = 17.4486
FEATURE [TechDraw::DrawViewBalloon] Balloon002
  BubbleShape = 0
  EndType = 0
  EndTypeScale = 1
  KinkLength = 5
  LockPosition = false
  OriginX = 23.8123
  OriginY = -20.3591
  Rotation = 0
  ScaleType = 0
  ShapeScale = 1
  SourceView = -> View021
  Text = 3
  TextWrapLen = -1
  X = 45.4442
  Y = 5.76069
FEATURE [TechDraw::DrawPage] Page005  label="Planos-floating-tank"
  KeepUpdated = true
  NextBalloonIndex = 4
  ProjectionType = 0
  Template = -> Template005
  Views = -> [View020,View001,View002,View021,Dimension001,Dimension003,Dimension004,Dimension005,Dimension007,Dimension008,Dimension009,Dimension100,Dimension010,Dimension011,Dimension012,Dimension013,Dimension014,Dimension015,Balloon012,Balloon013,Balloon002,Annotation002]
FEATURE [App::DocumentObjectGroup] Group  label="Planos001"
  Group = -> [Page004,Page003,Page,Page002,Balloon004,Page005]
note: 5 file-system paths scrubbed to <path> (originals preserved in the JSON sidecar)
